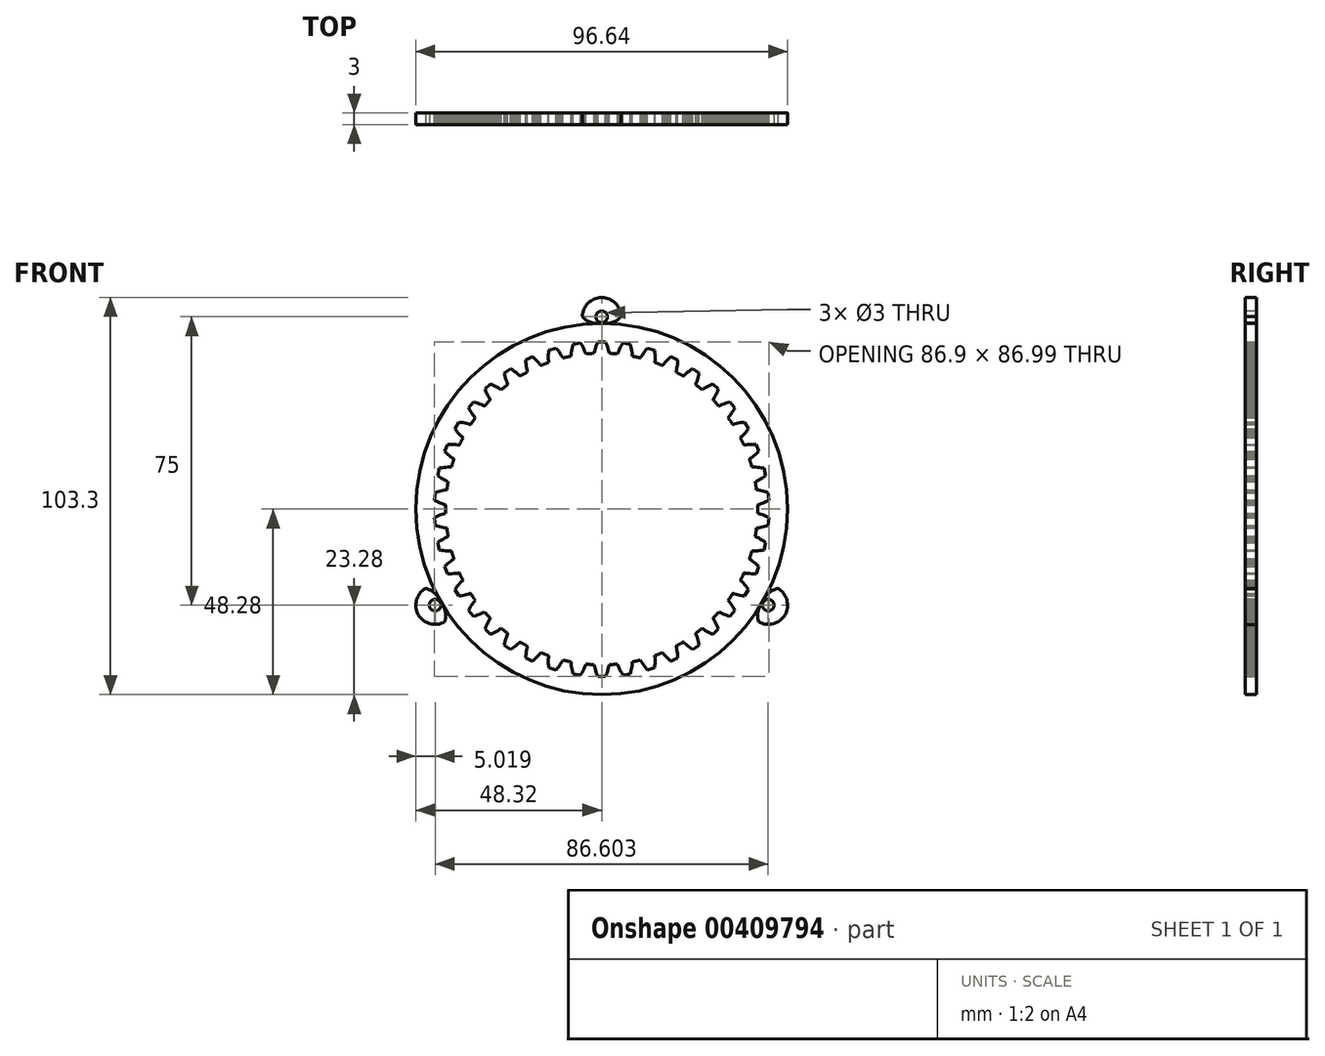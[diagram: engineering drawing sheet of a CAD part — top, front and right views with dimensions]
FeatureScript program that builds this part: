
annotation { "Feature Type Name" : "Feature", "Feature Type Description" : "" }
export const myFeature = defineFeature(function(context is Context, id is Id, definition is map)
    precondition{}
    {
        {
            var Q0;
            Q0=qCreatedBy(makeId("Front.planeOp"),FACE);
            var sketch = newSketch(context, id + "F0", { "sketchPlane" : qUnion([Q0])});
            skLineSegment(sketch, "E0", {"start": v(-40.42, 1.05) * mm, "end": v(-40.54, 1.09) * mm});
            skLineSegment(sketch, "E1", {"start": v(-40.54, 1.09) * mm, "end": v(-40.67, 1.12) * mm});
            skLineSegment(sketch, "E2", {"start": v(-40.67, 1.12) * mm, "end": v(-40.92, 1.2) * mm});
            skLineSegment(sketch, "E3", {"start": v(-40.92, 1.2) * mm, "end": v(-41.43, 1.36) * mm});
            skLineSegment(sketch, "E4", {"start": v(-41.43, 1.36) * mm, "end": v(-41.94, 1.56) * mm});
            skLineSegment(sketch, "E5", {"start": v(-41.94, 1.56) * mm, "end": v(-42.44, 1.77) * mm});
            skLineSegment(sketch, "E6", {"start": v(-42.44, 1.77) * mm, "end": v(-42.95, 2) * mm});
            skLineSegment(sketch, "E7", {"start": v(-42.95, 2) * mm, "end": v(-43.45, 2.26) * mm});
            skLineSegment(sketch, "E8", {"start": v(-43.45, 2.26) * mm, "end": v(-43.3, 4.24) * mm});
            skLineSegment(sketch, "E9", {"start": v(-43.3, 4.24) * mm, "end": v(-42.77, 4.42) * mm});
            skLineSegment(sketch, "E10", {"start": v(-42.77, 4.42) * mm, "end": v(-42.23, 4.57) * mm});
            skLineSegment(sketch, "E11", {"start": v(-42.23, 4.57) * mm, "end": v(-41.7, 4.71) * mm});
            skLineSegment(sketch, "E12", {"start": v(-41.7, 4.71) * mm, "end": v(-41.17, 4.83) * mm});
            skLineSegment(sketch, "E13", {"start": v(-41.17, 4.83) * mm, "end": v(-40.65, 4.92) * mm});
            skLineSegment(sketch, "E14", {"start": v(-40.65, 4.92) * mm, "end": v(-40.38, 4.95) * mm});
            skLineSegment(sketch, "E15", {"start": v(-40.38, 4.95) * mm, "end": v(-40.25, 4.97) * mm});
            skLineSegment(sketch, "E16", {"start": v(-40.25, 4.97) * mm, "end": v(-40.12, 4.98) * mm});
            skLineSegment(sketch, "E17", {"start": v(-40.12, 4.98) * mm, "end": v(-39.8, 7.06) * mm});
            skLineSegment(sketch, "E18", {"start": v(-39.8, 7.06) * mm, "end": v(-39.93, 7.12) * mm});
            skLineSegment(sketch, "E19", {"start": v(-39.93, 7.12) * mm, "end": v(-40.05, 7.17) * mm});
            skLineSegment(sketch, "E20", {"start": v(-40.05, 7.17) * mm, "end": v(-40.29, 7.28) * mm});
            skLineSegment(sketch, "E21", {"start": v(-40.29, 7.28) * mm, "end": v(-40.77, 7.52) * mm});
            skLineSegment(sketch, "E22", {"start": v(-40.77, 7.52) * mm, "end": v(-41.24, 7.8) * mm});
            skLineSegment(sketch, "E23", {"start": v(-41.24, 7.8) * mm, "end": v(-41.7, 8.08) * mm});
            skLineSegment(sketch, "E24", {"start": v(-41.7, 8.08) * mm, "end": v(-42.17, 8.39) * mm});
            skLineSegment(sketch, "E25", {"start": v(-42.17, 8.39) * mm, "end": v(-42.63, 8.71) * mm});
            skLineSegment(sketch, "E26", {"start": v(-42.63, 8.71) * mm, "end": v(-42.19, 10.64) * mm});
            skLineSegment(sketch, "E27", {"start": v(-42.19, 10.64) * mm, "end": v(-41.63, 10.74) * mm});
            skLineSegment(sketch, "E28", {"start": v(-41.63, 10.74) * mm, "end": v(-41.08, 10.82) * mm});
            skLineSegment(sketch, "E29", {"start": v(-41.08, 10.82) * mm, "end": v(-40.54, 10.87) * mm});
            skLineSegment(sketch, "E30", {"start": v(-40.54, 10.87) * mm, "end": v(-40, 10.9) * mm});
            skLineSegment(sketch, "E31", {"start": v(-40, 10.9) * mm, "end": v(-39.46, 10.92) * mm});
            skLineSegment(sketch, "E32", {"start": v(-39.46, 10.92) * mm, "end": v(-39.2, 10.92) * mm});
            skLineSegment(sketch, "E33", {"start": v(-39.2, 10.92) * mm, "end": v(-39.06, 10.91) * mm});
            skLineSegment(sketch, "E34", {"start": v(-39.06, 10.91) * mm, "end": v(-38.93, 10.9) * mm});
            skLineSegment(sketch, "E35", {"start": v(-38.93, 10.9) * mm, "end": v(-38.3, 12.92) * mm});
            skLineSegment(sketch, "E36", {"start": v(-38.3, 12.92) * mm, "end": v(-38.42, 12.99) * mm});
            skLineSegment(sketch, "E37", {"start": v(-38.42, 12.99) * mm, "end": v(-38.53, 13.06) * mm});
            skLineSegment(sketch, "E38", {"start": v(-38.53, 13.06) * mm, "end": v(-38.75, 13.2) * mm});
            skLineSegment(sketch, "E39", {"start": v(-38.75, 13.2) * mm, "end": v(-39.19, 13.52) * mm});
            skLineSegment(sketch, "E40", {"start": v(-39.19, 13.52) * mm, "end": v(-39.62, 13.85) * mm});
            skLineSegment(sketch, "E41", {"start": v(-39.62, 13.85) * mm, "end": v(-40.04, 14.2) * mm});
            skLineSegment(sketch, "E42", {"start": v(-40.04, 14.2) * mm, "end": v(-40.45, 14.58) * mm});
            skLineSegment(sketch, "E43", {"start": v(-40.45, 14.58) * mm, "end": v(-40.85, 14.97) * mm});
            skLineSegment(sketch, "E44", {"start": v(-40.85, 14.97) * mm, "end": v(-40.13, 16.81) * mm});
            skLineSegment(sketch, "E45", {"start": v(-40.13, 16.81) * mm, "end": v(-39.57, 16.82) * mm});
            skLineSegment(sketch, "E46", {"start": v(-39.57, 16.82) * mm, "end": v(-39.01, 16.82) * mm});
            skLineSegment(sketch, "E47", {"start": v(-39.01, 16.82) * mm, "end": v(-38.46, 16.8) * mm});
            skLineSegment(sketch, "E48", {"start": v(-38.46, 16.8) * mm, "end": v(-37.92, 16.75) * mm});
            skLineSegment(sketch, "E49", {"start": v(-37.92, 16.75) * mm, "end": v(-37.4, 16.68) * mm});
            skLineSegment(sketch, "E50", {"start": v(-37.4, 16.68) * mm, "end": v(-37.13, 16.64) * mm});
            skLineSegment(sketch, "E51", {"start": v(-37.13, 16.64) * mm, "end": v(-37, 16.61) * mm});
            skLineSegment(sketch, "E52", {"start": v(-37, 16.61) * mm, "end": v(-36.87, 16.59) * mm});
            skLineSegment(sketch, "E53", {"start": v(-36.87, 16.59) * mm, "end": v(-35.96, 18.48) * mm});
            skLineSegment(sketch, "E54", {"start": v(-35.96, 18.48) * mm, "end": v(-36.06, 18.57) * mm});
            skLineSegment(sketch, "E55", {"start": v(-36.06, 18.57) * mm, "end": v(-36.16, 18.66) * mm});
            skLineSegment(sketch, "E56", {"start": v(-36.16, 18.66) * mm, "end": v(-36.35, 18.83) * mm});
            skLineSegment(sketch, "E57", {"start": v(-36.35, 18.83) * mm, "end": v(-36.74, 19.2) * mm});
            skLineSegment(sketch, "E58", {"start": v(-36.74, 19.2) * mm, "end": v(-37.11, 19.6) * mm});
            skLineSegment(sketch, "E59", {"start": v(-37.11, 19.6) * mm, "end": v(-37.47, 20.01) * mm});
            skLineSegment(sketch, "E60", {"start": v(-37.47, 20.01) * mm, "end": v(-37.82, 20.44) * mm});
            skLineSegment(sketch, "E61", {"start": v(-37.82, 20.44) * mm, "end": v(-38.16, 20.9) * mm});
            skLineSegment(sketch, "E62", {"start": v(-38.16, 20.9) * mm, "end": v(-37.17, 22.6) * mm});
            skLineSegment(sketch, "E63", {"start": v(-37.17, 22.6) * mm, "end": v(-36.62, 22.53) * mm});
            skLineSegment(sketch, "E64", {"start": v(-36.62, 22.53) * mm, "end": v(-36.07, 22.44) * mm});
            skLineSegment(sketch, "E65", {"start": v(-36.07, 22.44) * mm, "end": v(-35.53, 22.34) * mm});
            skLineSegment(sketch, "E66", {"start": v(-35.53, 22.34) * mm, "end": v(-35, 22.21) * mm});
            skLineSegment(sketch, "E67", {"start": v(-35, 22.21) * mm, "end": v(-34.49, 22.07) * mm});
            skLineSegment(sketch, "E68", {"start": v(-34.49, 22.07) * mm, "end": v(-34.23, 21.98) * mm});
            skLineSegment(sketch, "E69", {"start": v(-34.23, 21.98) * mm, "end": v(-34.1, 21.94) * mm});
            skLineSegment(sketch, "E70", {"start": v(-34.1, 21.94) * mm, "end": v(-33.99, 21.9) * mm});
            skLineSegment(sketch, "E71", {"start": v(-33.99, 21.9) * mm, "end": v(-32.8, 23.64) * mm});
            skLineSegment(sketch, "E72", {"start": v(-32.8, 23.64) * mm, "end": v(-32.89, 23.74) * mm});
            skLineSegment(sketch, "E73", {"start": v(-32.89, 23.74) * mm, "end": v(-32.97, 23.84) * mm});
            skLineSegment(sketch, "E74", {"start": v(-32.97, 23.84) * mm, "end": v(-33.14, 24.04) * mm});
            skLineSegment(sketch, "E75", {"start": v(-33.14, 24.04) * mm, "end": v(-33.46, 24.47) * mm});
            skLineSegment(sketch, "E76", {"start": v(-33.46, 24.47) * mm, "end": v(-33.77, 24.91) * mm});
            skLineSegment(sketch, "E77", {"start": v(-33.77, 24.91) * mm, "end": v(-34.07, 25.37) * mm});
            skLineSegment(sketch, "E78", {"start": v(-34.07, 25.37) * mm, "end": v(-34.35, 25.85) * mm});
            skLineSegment(sketch, "E79", {"start": v(-34.35, 25.85) * mm, "end": v(-34.62, 26.35) * mm});
            skLineSegment(sketch, "E80", {"start": v(-34.62, 26.35) * mm, "end": v(-33.39, 27.9) * mm});
            skLineSegment(sketch, "E81", {"start": v(-33.39, 27.9) * mm, "end": v(-32.85, 27.74) * mm});
            skLineSegment(sketch, "E82", {"start": v(-32.85, 27.74) * mm, "end": v(-32.32, 27.57) * mm});
            skLineSegment(sketch, "E83", {"start": v(-32.32, 27.57) * mm, "end": v(-31.8, 27.38) * mm});
            skLineSegment(sketch, "E84", {"start": v(-31.8, 27.38) * mm, "end": v(-31.3, 27.18) * mm});
            skLineSegment(sketch, "E85", {"start": v(-31.3, 27.18) * mm, "end": v(-30.81, 26.96) * mm});
            skLineSegment(sketch, "E86", {"start": v(-30.81, 26.96) * mm, "end": v(-30.58, 26.84) * mm});
            skLineSegment(sketch, "E87", {"start": v(-30.58, 26.84) * mm, "end": v(-30.46, 26.78) * mm});
            skLineSegment(sketch, "E88", {"start": v(-30.46, 26.78) * mm, "end": v(-30.34, 26.72) * mm});
            skLineSegment(sketch, "E89", {"start": v(-30.34, 26.72) * mm, "end": v(-28.91, 28.26) * mm});
            skLineSegment(sketch, "E90", {"start": v(-28.91, 28.26) * mm, "end": v(-28.98, 28.37) * mm});
            skLineSegment(sketch, "E91", {"start": v(-28.98, 28.37) * mm, "end": v(-29.05, 28.48) * mm});
            skLineSegment(sketch, "E92", {"start": v(-29.05, 28.48) * mm, "end": v(-29.19, 28.71) * mm});
            skLineSegment(sketch, "E93", {"start": v(-29.19, 28.71) * mm, "end": v(-29.44, 29.18) * mm});
            skLineSegment(sketch, "E94", {"start": v(-29.44, 29.18) * mm, "end": v(-29.68, 29.67) * mm});
            skLineSegment(sketch, "E95", {"start": v(-29.68, 29.67) * mm, "end": v(-29.9, 30.17) * mm});
            skLineSegment(sketch, "E96", {"start": v(-29.9, 30.17) * mm, "end": v(-30.12, 30.68) * mm});
            skLineSegment(sketch, "E97", {"start": v(-30.12, 30.68) * mm, "end": v(-30.31, 31.21) * mm});
            skLineSegment(sketch, "E98", {"start": v(-30.31, 31.21) * mm, "end": v(-28.86, 32.56) * mm});
            skLineSegment(sketch, "E99", {"start": v(-28.86, 32.56) * mm, "end": v(-28.35, 32.33) * mm});
            skLineSegment(sketch, "E100", {"start": v(-28.35, 32.33) * mm, "end": v(-27.85, 32.08) * mm});
            skLineSegment(sketch, "E101", {"start": v(-27.85, 32.08) * mm, "end": v(-27.37, 31.82) * mm});
            skLineSegment(sketch, "E102", {"start": v(-27.37, 31.82) * mm, "end": v(-26.9, 31.54) * mm});
            skLineSegment(sketch, "E103", {"start": v(-26.9, 31.54) * mm, "end": v(-26.45, 31.25) * mm});
            skLineSegment(sketch, "E104", {"start": v(-26.45, 31.25) * mm, "end": v(-26.23, 31.1) * mm});
            skLineSegment(sketch, "E105", {"start": v(-26.23, 31.1) * mm, "end": v(-26.13, 31.02) * mm});
            skLineSegment(sketch, "E106", {"start": v(-26.13, 31.02) * mm, "end": v(-26.02, 30.94) * mm});
            skLineSegment(sketch, "E107", {"start": v(-26.02, 30.94) * mm, "end": v(-24.38, 32.25) * mm});
            skLineSegment(sketch, "E108", {"start": v(-24.38, 32.25) * mm, "end": v(-24.43, 32.37) * mm});
            skLineSegment(sketch, "E109", {"start": v(-24.43, 32.37) * mm, "end": v(-24.48, 32.5) * mm});
            skLineSegment(sketch, "E110", {"start": v(-24.48, 32.5) * mm, "end": v(-24.58, 32.74) * mm});
            skLineSegment(sketch, "E111", {"start": v(-24.58, 32.74) * mm, "end": v(-24.77, 33.24) * mm});
            skLineSegment(sketch, "E112", {"start": v(-24.77, 33.24) * mm, "end": v(-24.93, 33.76) * mm});
            skLineSegment(sketch, "E113", {"start": v(-24.93, 33.76) * mm, "end": v(-25.08, 34.29) * mm});
            skLineSegment(sketch, "E114", {"start": v(-25.08, 34.29) * mm, "end": v(-25.2, 34.83) * mm});
            skLineSegment(sketch, "E115", {"start": v(-25.2, 34.83) * mm, "end": v(-25.32, 35.38) * mm});
            skLineSegment(sketch, "E116", {"start": v(-25.32, 35.38) * mm, "end": v(-23.68, 36.5) * mm});
            skLineSegment(sketch, "E117", {"start": v(-23.68, 36.5) * mm, "end": v(-23.21, 36.19) * mm});
            skLineSegment(sketch, "E118", {"start": v(-23.21, 36.19) * mm, "end": v(-22.76, 35.87) * mm});
            skLineSegment(sketch, "E119", {"start": v(-22.76, 35.87) * mm, "end": v(-22.32, 35.54) * mm});
            skLineSegment(sketch, "E120", {"start": v(-22.32, 35.54) * mm, "end": v(-21.9, 35.2) * mm});
            skLineSegment(sketch, "E121", {"start": v(-21.9, 35.2) * mm, "end": v(-21.5, 34.84) * mm});
            skLineSegment(sketch, "E122", {"start": v(-21.5, 34.84) * mm, "end": v(-21.3, 34.66) * mm});
            skLineSegment(sketch, "E123", {"start": v(-21.3, 34.66) * mm, "end": v(-21.21, 34.57) * mm});
            skLineSegment(sketch, "E124", {"start": v(-21.21, 34.57) * mm, "end": v(-21.12, 34.47) * mm});
            skLineSegment(sketch, "E125", {"start": v(-21.12, 34.47) * mm, "end": v(-19.3, 35.53) * mm});
            skLineSegment(sketch, "E126", {"start": v(-19.3, 35.53) * mm, "end": v(-19.33, 35.65) * mm});
            skLineSegment(sketch, "E127", {"start": v(-19.33, 35.65) * mm, "end": v(-19.36, 35.78) * mm});
            skLineSegment(sketch, "E128", {"start": v(-19.36, 35.78) * mm, "end": v(-19.43, 36.04) * mm});
            skLineSegment(sketch, "E129", {"start": v(-19.43, 36.04) * mm, "end": v(-19.53, 36.56) * mm});
            skLineSegment(sketch, "E130", {"start": v(-19.53, 36.56) * mm, "end": v(-19.62, 37.1) * mm});
            skLineSegment(sketch, "E131", {"start": v(-19.62, 37.1) * mm, "end": v(-19.69, 37.64) * mm});
            skLineSegment(sketch, "E132", {"start": v(-19.69, 37.64) * mm, "end": v(-19.73, 38.2) * mm});
            skLineSegment(sketch, "E133", {"start": v(-19.73, 38.2) * mm, "end": v(-19.76, 38.76) * mm});
            skLineSegment(sketch, "E134", {"start": v(-19.76, 38.76) * mm, "end": v(-17.98, 39.62) * mm});
            skLineSegment(sketch, "E135", {"start": v(-17.98, 39.62) * mm, "end": v(-17.56, 39.24) * mm});
            skLineSegment(sketch, "E136", {"start": v(-17.56, 39.24) * mm, "end": v(-17.16, 38.86) * mm});
            skLineSegment(sketch, "E137", {"start": v(-17.16, 38.86) * mm, "end": v(-16.77, 38.47) * mm});
            skLineSegment(sketch, "E138", {"start": v(-16.77, 38.47) * mm, "end": v(-16.4, 38.07) * mm});
            skLineSegment(sketch, "E139", {"start": v(-16.4, 38.07) * mm, "end": v(-16.06, 37.66) * mm});
            skLineSegment(sketch, "E140", {"start": v(-16.06, 37.66) * mm, "end": v(-15.9, 37.45) * mm});
            skLineSegment(sketch, "E141", {"start": v(-15.9, 37.45) * mm, "end": v(-15.82, 37.34) * mm});
            skLineSegment(sketch, "E142", {"start": v(-15.82, 37.34) * mm, "end": v(-15.75, 37.24) * mm});
            skLineSegment(sketch, "E143", {"start": v(-15.75, 37.24) * mm, "end": v(-13.79, 38) * mm});
            skLineSegment(sketch, "E144", {"start": v(-13.79, 38) * mm, "end": v(-13.8, 38.14) * mm});
            skLineSegment(sketch, "E145", {"start": v(-13.8, 38.14) * mm, "end": v(-13.82, 38.27) * mm});
            skLineSegment(sketch, "E146", {"start": v(-13.82, 38.27) * mm, "end": v(-13.84, 38.53) * mm});
            skLineSegment(sketch, "E147", {"start": v(-13.84, 38.53) * mm, "end": v(-13.87, 39.07) * mm});
            skLineSegment(sketch, "E148", {"start": v(-13.87, 39.07) * mm, "end": v(-13.87, 39.6) * mm});
            skLineSegment(sketch, "E149", {"start": v(-13.87, 39.6) * mm, "end": v(-13.86, 40.16) * mm});
            skLineSegment(sketch, "E150", {"start": v(-13.86, 40.16) * mm, "end": v(-13.82, 40.71) * mm});
            skLineSegment(sketch, "E151", {"start": v(-13.82, 40.71) * mm, "end": v(-13.77, 41.27) * mm});
            skLineSegment(sketch, "E152", {"start": v(-13.77, 41.27) * mm, "end": v(-11.87, 41.86) * mm});
            skLineSegment(sketch, "E153", {"start": v(-11.87, 41.86) * mm, "end": v(-11.51, 41.42) * mm});
            skLineSegment(sketch, "E154", {"start": v(-11.51, 41.42) * mm, "end": v(-11.17, 40.99) * mm});
            skLineSegment(sketch, "E155", {"start": v(-11.17, 40.99) * mm, "end": v(-10.85, 40.54) * mm});
            skLineSegment(sketch, "E156", {"start": v(-10.85, 40.54) * mm, "end": v(-10.55, 40.1) * mm});
            skLineSegment(sketch, "E157", {"start": v(-10.55, 40.1) * mm, "end": v(-10.27, 39.63) * mm});
            skLineSegment(sketch, "E158", {"start": v(-10.27, 39.63) * mm, "end": v(-10.14, 39.4) * mm});
            skLineSegment(sketch, "E159", {"start": v(-10.14, 39.4) * mm, "end": v(-10.08, 39.28) * mm});
            skLineSegment(sketch, "E160", {"start": v(-10.08, 39.28) * mm, "end": v(-10.02, 39.17) * mm});
            skLineSegment(sketch, "E161", {"start": v(-10.02, 39.17) * mm, "end": v(-7.97, 39.64) * mm});
            skLineSegment(sketch, "E162", {"start": v(-7.97, 39.64) * mm, "end": v(-7.96, 39.77) * mm});
            skLineSegment(sketch, "E163", {"start": v(-7.96, 39.77) * mm, "end": v(-7.96, 39.9) * mm});
            skLineSegment(sketch, "E164", {"start": v(-7.96, 39.9) * mm, "end": v(-7.94, 40.16) * mm});
            skLineSegment(sketch, "E165", {"start": v(-7.94, 40.16) * mm, "end": v(-7.89, 40.7) * mm});
            skLineSegment(sketch, "E166", {"start": v(-7.89, 40.7) * mm, "end": v(-7.81, 41.23) * mm});
            skLineSegment(sketch, "E167", {"start": v(-7.81, 41.23) * mm, "end": v(-7.72, 41.77) * mm});
            skLineSegment(sketch, "E168", {"start": v(-7.72, 41.77) * mm, "end": v(-7.6, 42.32) * mm});
            skLineSegment(sketch, "E169", {"start": v(-7.6, 42.32) * mm, "end": v(-7.46, 42.86) * mm});
            skLineSegment(sketch, "E170", {"start": v(-7.46, 42.86) * mm, "end": v(-5.5, 43.16) * mm});
            skLineSegment(sketch, "E171", {"start": v(-5.5, 43.16) * mm, "end": v(-5.21, 42.68) * mm});
            skLineSegment(sketch, "E172", {"start": v(-5.21, 42.68) * mm, "end": v(-4.94, 42.2) * mm});
            skLineSegment(sketch, "E173", {"start": v(-4.94, 42.2) * mm, "end": v(-4.69, 41.7) * mm});
            skLineSegment(sketch, "E174", {"start": v(-4.69, 41.7) * mm, "end": v(-4.46, 41.21) * mm});
            skLineSegment(sketch, "E175", {"start": v(-4.46, 41.21) * mm, "end": v(-4.25, 40.72) * mm});
            skLineSegment(sketch, "E176", {"start": v(-4.25, 40.72) * mm, "end": v(-4.16, 40.47) * mm});
            skLineSegment(sketch, "E177", {"start": v(-4.16, 40.47) * mm, "end": v(-4.11, 40.35) * mm});
            skLineSegment(sketch, "E178", {"start": v(-4.11, 40.35) * mm, "end": v(-4.07, 40.22) * mm});
            skLineSegment(sketch, "E179", {"start": v(-4.07, 40.22) * mm, "end": v(-1.97, 40.38) * mm});
            skLineSegment(sketch, "E180", {"start": v(-1.97, 40.38) * mm, "end": v(-1.95, 40.51) * mm});
            skLineSegment(sketch, "E181", {"start": v(-1.95, 40.51) * mm, "end": v(-1.92, 40.64) * mm});
            skLineSegment(sketch, "E182", {"start": v(-1.92, 40.64) * mm, "end": v(-1.87, 40.9) * mm});
            skLineSegment(sketch, "E183", {"start": v(-1.87, 40.9) * mm, "end": v(-1.74, 41.42) * mm});
            skLineSegment(sketch, "E184", {"start": v(-1.74, 41.42) * mm, "end": v(-1.58, 41.94) * mm});
            skLineSegment(sketch, "E185", {"start": v(-1.58, 41.94) * mm, "end": v(-1.4, 42.46) * mm});
            skLineSegment(sketch, "E186", {"start": v(-1.4, 42.46) * mm, "end": v(-1.2, 42.98) * mm});
            skLineSegment(sketch, "E187", {"start": v(-1.2, 42.98) * mm, "end": v(-0.99, 43.5) * mm});
            skLineSegment(sketch, "E188", {"start": v(-0.99, 43.5) * mm, "end": v(0.99, 43.5) * mm});
            skLineSegment(sketch, "E189", {"start": v(0.99, 43.5) * mm, "end": v(1.2, 42.98) * mm});
            skLineSegment(sketch, "E190", {"start": v(1.2, 42.98) * mm, "end": v(1.4, 42.46) * mm});
            skLineSegment(sketch, "E191", {"start": v(1.4, 42.46) * mm, "end": v(1.58, 41.94) * mm});
            skLineSegment(sketch, "E192", {"start": v(1.58, 41.94) * mm, "end": v(1.74, 41.42) * mm});
            skLineSegment(sketch, "E193", {"start": v(1.74, 41.42) * mm, "end": v(1.87, 40.9) * mm});
            skLineSegment(sketch, "E194", {"start": v(1.87, 40.9) * mm, "end": v(1.92, 40.64) * mm});
            skLineSegment(sketch, "E195", {"start": v(1.92, 40.64) * mm, "end": v(1.95, 40.51) * mm});
            skLineSegment(sketch, "E196", {"start": v(1.95, 40.51) * mm, "end": v(1.97, 40.38) * mm});
            skLineSegment(sketch, "E197", {"start": v(1.97, 40.38) * mm, "end": v(4.07, 40.22) * mm});
            skLineSegment(sketch, "E198", {"start": v(4.07, 40.22) * mm, "end": v(4.11, 40.35) * mm});
            skLineSegment(sketch, "E199", {"start": v(4.11, 40.35) * mm, "end": v(4.16, 40.47) * mm});
            skLineSegment(sketch, "E200", {"start": v(4.16, 40.47) * mm, "end": v(4.25, 40.72) * mm});
            skLineSegment(sketch, "E201", {"start": v(4.25, 40.72) * mm, "end": v(4.46, 41.21) * mm});
            skLineSegment(sketch, "E202", {"start": v(4.46, 41.21) * mm, "end": v(4.69, 41.7) * mm});
            skLineSegment(sketch, "E203", {"start": v(4.69, 41.7) * mm, "end": v(4.94, 42.2) * mm});
            skLineSegment(sketch, "E204", {"start": v(4.94, 42.2) * mm, "end": v(5.21, 42.68) * mm});
            skLineSegment(sketch, "E205", {"start": v(5.21, 42.68) * mm, "end": v(5.5, 43.16) * mm});
            skLineSegment(sketch, "E206", {"start": v(5.5, 43.16) * mm, "end": v(7.46, 42.86) * mm});
            skLineSegment(sketch, "E207", {"start": v(7.46, 42.86) * mm, "end": v(7.6, 42.32) * mm});
            skLineSegment(sketch, "E208", {"start": v(7.6, 42.32) * mm, "end": v(7.72, 41.77) * mm});
            skLineSegment(sketch, "E209", {"start": v(7.72, 41.77) * mm, "end": v(7.81, 41.23) * mm});
            skLineSegment(sketch, "E210", {"start": v(7.81, 41.23) * mm, "end": v(7.89, 40.7) * mm});
            skLineSegment(sketch, "E211", {"start": v(7.89, 40.7) * mm, "end": v(7.94, 40.16) * mm});
            skLineSegment(sketch, "E212", {"start": v(7.94, 40.16) * mm, "end": v(7.96, 39.9) * mm});
            skLineSegment(sketch, "E213", {"start": v(7.96, 39.9) * mm, "end": v(7.96, 39.77) * mm});
            skLineSegment(sketch, "E214", {"start": v(7.96, 39.77) * mm, "end": v(7.97, 39.64) * mm});
            skLineSegment(sketch, "E215", {"start": v(7.97, 39.64) * mm, "end": v(10.02, 39.17) * mm});
            skLineSegment(sketch, "E216", {"start": v(10.02, 39.17) * mm, "end": v(10.08, 39.28) * mm});
            skLineSegment(sketch, "E217", {"start": v(10.08, 39.28) * mm, "end": v(10.14, 39.4) * mm});
            skLineSegment(sketch, "E218", {"start": v(10.14, 39.4) * mm, "end": v(10.27, 39.63) * mm});
            skLineSegment(sketch, "E219", {"start": v(10.27, 39.63) * mm, "end": v(10.55, 40.1) * mm});
            skLineSegment(sketch, "E220", {"start": v(10.55, 40.1) * mm, "end": v(10.85, 40.54) * mm});
            skLineSegment(sketch, "E221", {"start": v(10.85, 40.54) * mm, "end": v(11.17, 40.99) * mm});
            skLineSegment(sketch, "E222", {"start": v(11.17, 40.99) * mm, "end": v(11.51, 41.42) * mm});
            skLineSegment(sketch, "E223", {"start": v(11.51, 41.42) * mm, "end": v(11.87, 41.86) * mm});
            skLineSegment(sketch, "E224", {"start": v(11.87, 41.86) * mm, "end": v(13.77, 41.27) * mm});
            skLineSegment(sketch, "E225", {"start": v(13.77, 41.27) * mm, "end": v(13.82, 40.71) * mm});
            skLineSegment(sketch, "E226", {"start": v(13.82, 40.71) * mm, "end": v(13.86, 40.16) * mm});
            skLineSegment(sketch, "E227", {"start": v(13.86, 40.16) * mm, "end": v(13.87, 39.6) * mm});
            skLineSegment(sketch, "E228", {"start": v(13.87, 39.6) * mm, "end": v(13.87, 39.07) * mm});
            skLineSegment(sketch, "E229", {"start": v(13.87, 39.07) * mm, "end": v(13.84, 38.53) * mm});
            skLineSegment(sketch, "E230", {"start": v(13.84, 38.53) * mm, "end": v(13.82, 38.27) * mm});
            skLineSegment(sketch, "E231", {"start": v(13.82, 38.27) * mm, "end": v(13.8, 38.14) * mm});
            skLineSegment(sketch, "E232", {"start": v(13.8, 38.14) * mm, "end": v(13.79, 38) * mm});
            skLineSegment(sketch, "E233", {"start": v(13.79, 38) * mm, "end": v(15.75, 37.24) * mm});
            skLineSegment(sketch, "E234", {"start": v(15.75, 37.24) * mm, "end": v(15.82, 37.34) * mm});
            skLineSegment(sketch, "E235", {"start": v(15.82, 37.34) * mm, "end": v(15.9, 37.45) * mm});
            skLineSegment(sketch, "E236", {"start": v(15.9, 37.45) * mm, "end": v(16.06, 37.66) * mm});
            skLineSegment(sketch, "E237", {"start": v(16.06, 37.66) * mm, "end": v(16.4, 38.07) * mm});
            skLineSegment(sketch, "E238", {"start": v(16.4, 38.07) * mm, "end": v(16.77, 38.47) * mm});
            skLineSegment(sketch, "E239", {"start": v(16.77, 38.47) * mm, "end": v(17.16, 38.86) * mm});
            skLineSegment(sketch, "E240", {"start": v(17.16, 38.86) * mm, "end": v(17.56, 39.24) * mm});
            skLineSegment(sketch, "E241", {"start": v(17.56, 39.24) * mm, "end": v(17.98, 39.62) * mm});
            skLineSegment(sketch, "E242", {"start": v(17.98, 39.62) * mm, "end": v(19.76, 38.76) * mm});
            skLineSegment(sketch, "E243", {"start": v(19.76, 38.76) * mm, "end": v(19.73, 38.2) * mm});
            skLineSegment(sketch, "E244", {"start": v(19.73, 38.2) * mm, "end": v(19.69, 37.64) * mm});
            skLineSegment(sketch, "E245", {"start": v(19.69, 37.64) * mm, "end": v(19.62, 37.1) * mm});
            skLineSegment(sketch, "E246", {"start": v(19.62, 37.1) * mm, "end": v(19.53, 36.56) * mm});
            skLineSegment(sketch, "E247", {"start": v(19.53, 36.56) * mm, "end": v(19.43, 36.04) * mm});
            skLineSegment(sketch, "E248", {"start": v(19.43, 36.04) * mm, "end": v(19.36, 35.78) * mm});
            skLineSegment(sketch, "E249", {"start": v(19.36, 35.78) * mm, "end": v(19.33, 35.65) * mm});
            skLineSegment(sketch, "E250", {"start": v(19.33, 35.65) * mm, "end": v(19.3, 35.53) * mm});
            skLineSegment(sketch, "E251", {"start": v(19.3, 35.53) * mm, "end": v(21.12, 34.47) * mm});
            skLineSegment(sketch, "E252", {"start": v(21.12, 34.47) * mm, "end": v(21.21, 34.57) * mm});
            skLineSegment(sketch, "E253", {"start": v(21.21, 34.57) * mm, "end": v(21.3, 34.66) * mm});
            skLineSegment(sketch, "E254", {"start": v(21.3, 34.66) * mm, "end": v(21.5, 34.84) * mm});
            skLineSegment(sketch, "E255", {"start": v(21.5, 34.84) * mm, "end": v(21.9, 35.2) * mm});
            skLineSegment(sketch, "E256", {"start": v(21.9, 35.2) * mm, "end": v(22.32, 35.54) * mm});
            skLineSegment(sketch, "E257", {"start": v(22.32, 35.54) * mm, "end": v(22.76, 35.87) * mm});
            skLineSegment(sketch, "E258", {"start": v(22.76, 35.87) * mm, "end": v(23.21, 36.19) * mm});
            skLineSegment(sketch, "E259", {"start": v(23.21, 36.19) * mm, "end": v(23.68, 36.5) * mm});
            skLineSegment(sketch, "E260", {"start": v(23.68, 36.5) * mm, "end": v(25.32, 35.38) * mm});
            skLineSegment(sketch, "E261", {"start": v(25.32, 35.38) * mm, "end": v(25.2, 34.83) * mm});
            skLineSegment(sketch, "E262", {"start": v(25.2, 34.83) * mm, "end": v(25.08, 34.29) * mm});
            skLineSegment(sketch, "E263", {"start": v(25.08, 34.29) * mm, "end": v(24.93, 33.76) * mm});
            skLineSegment(sketch, "E264", {"start": v(24.93, 33.76) * mm, "end": v(24.77, 33.24) * mm});
            skLineSegment(sketch, "E265", {"start": v(24.77, 33.24) * mm, "end": v(24.58, 32.74) * mm});
            skLineSegment(sketch, "E266", {"start": v(24.58, 32.74) * mm, "end": v(24.48, 32.5) * mm});
            skLineSegment(sketch, "E267", {"start": v(24.48, 32.5) * mm, "end": v(24.43, 32.37) * mm});
            skLineSegment(sketch, "E268", {"start": v(24.43, 32.37) * mm, "end": v(24.38, 32.25) * mm});
            skLineSegment(sketch, "E269", {"start": v(24.38, 32.25) * mm, "end": v(26.02, 30.94) * mm});
            skLineSegment(sketch, "E270", {"start": v(26.02, 30.94) * mm, "end": v(26.13, 31.02) * mm});
            skLineSegment(sketch, "E271", {"start": v(26.13, 31.02) * mm, "end": v(26.23, 31.1) * mm});
            skLineSegment(sketch, "E272", {"start": v(26.23, 31.1) * mm, "end": v(26.45, 31.25) * mm});
            skLineSegment(sketch, "E273", {"start": v(26.45, 31.25) * mm, "end": v(26.9, 31.54) * mm});
            skLineSegment(sketch, "E274", {"start": v(26.9, 31.54) * mm, "end": v(27.37, 31.82) * mm});
            skLineSegment(sketch, "E275", {"start": v(27.37, 31.82) * mm, "end": v(27.85, 32.08) * mm});
            skLineSegment(sketch, "E276", {"start": v(27.85, 32.08) * mm, "end": v(28.35, 32.33) * mm});
            skLineSegment(sketch, "E277", {"start": v(28.35, 32.33) * mm, "end": v(28.86, 32.56) * mm});
            skLineSegment(sketch, "E278", {"start": v(28.86, 32.56) * mm, "end": v(30.31, 31.21) * mm});
            skLineSegment(sketch, "E279", {"start": v(30.31, 31.21) * mm, "end": v(30.12, 30.68) * mm});
            skLineSegment(sketch, "E280", {"start": v(30.12, 30.68) * mm, "end": v(29.9, 30.17) * mm});
            skLineSegment(sketch, "E281", {"start": v(29.9, 30.17) * mm, "end": v(29.68, 29.67) * mm});
            skLineSegment(sketch, "E282", {"start": v(29.68, 29.67) * mm, "end": v(29.44, 29.18) * mm});
            skLineSegment(sketch, "E283", {"start": v(29.44, 29.18) * mm, "end": v(29.19, 28.71) * mm});
            skLineSegment(sketch, "E284", {"start": v(29.19, 28.71) * mm, "end": v(29.05, 28.48) * mm});
            skLineSegment(sketch, "E285", {"start": v(29.05, 28.48) * mm, "end": v(28.98, 28.37) * mm});
            skLineSegment(sketch, "E286", {"start": v(28.98, 28.37) * mm, "end": v(28.91, 28.26) * mm});
            skLineSegment(sketch, "E287", {"start": v(28.91, 28.26) * mm, "end": v(30.34, 26.72) * mm});
            skLineSegment(sketch, "E288", {"start": v(30.34, 26.72) * mm, "end": v(30.46, 26.78) * mm});
            skLineSegment(sketch, "E289", {"start": v(30.46, 26.78) * mm, "end": v(30.58, 26.84) * mm});
            skLineSegment(sketch, "E290", {"start": v(30.58, 26.84) * mm, "end": v(30.81, 26.96) * mm});
            skLineSegment(sketch, "E291", {"start": v(30.81, 26.96) * mm, "end": v(31.3, 27.18) * mm});
            skLineSegment(sketch, "E292", {"start": v(31.3, 27.18) * mm, "end": v(31.8, 27.38) * mm});
            skLineSegment(sketch, "E293", {"start": v(31.8, 27.38) * mm, "end": v(32.32, 27.57) * mm});
            skLineSegment(sketch, "E294", {"start": v(32.32, 27.57) * mm, "end": v(32.85, 27.74) * mm});
            skLineSegment(sketch, "E295", {"start": v(32.85, 27.74) * mm, "end": v(33.39, 27.9) * mm});
            skLineSegment(sketch, "E296", {"start": v(33.39, 27.9) * mm, "end": v(34.62, 26.35) * mm});
            skLineSegment(sketch, "E297", {"start": v(34.62, 26.35) * mm, "end": v(34.35, 25.85) * mm});
            skLineSegment(sketch, "E298", {"start": v(34.35, 25.85) * mm, "end": v(34.07, 25.37) * mm});
            skLineSegment(sketch, "E299", {"start": v(34.07, 25.37) * mm, "end": v(33.77, 24.91) * mm});
            skLineSegment(sketch, "E300", {"start": v(33.77, 24.91) * mm, "end": v(33.46, 24.47) * mm});
            skLineSegment(sketch, "E301", {"start": v(33.46, 24.47) * mm, "end": v(33.14, 24.04) * mm});
            skLineSegment(sketch, "E302", {"start": v(33.14, 24.04) * mm, "end": v(32.97, 23.84) * mm});
            skLineSegment(sketch, "E303", {"start": v(32.97, 23.84) * mm, "end": v(32.89, 23.74) * mm});
            skLineSegment(sketch, "E304", {"start": v(32.89, 23.74) * mm, "end": v(32.8, 23.64) * mm});
            skLineSegment(sketch, "E305", {"start": v(32.8, 23.64) * mm, "end": v(33.99, 21.9) * mm});
            skLineSegment(sketch, "E306", {"start": v(33.99, 21.9) * mm, "end": v(34.1, 21.94) * mm});
            skLineSegment(sketch, "E307", {"start": v(34.1, 21.94) * mm, "end": v(34.23, 21.98) * mm});
            skLineSegment(sketch, "E308", {"start": v(34.23, 21.98) * mm, "end": v(34.49, 22.07) * mm});
            skLineSegment(sketch, "E309", {"start": v(34.49, 22.07) * mm, "end": v(35, 22.21) * mm});
            skLineSegment(sketch, "E310", {"start": v(35, 22.21) * mm, "end": v(35.53, 22.34) * mm});
            skLineSegment(sketch, "E311", {"start": v(35.53, 22.34) * mm, "end": v(36.07, 22.44) * mm});
            skLineSegment(sketch, "E312", {"start": v(36.07, 22.44) * mm, "end": v(36.62, 22.53) * mm});
            skLineSegment(sketch, "E313", {"start": v(36.62, 22.53) * mm, "end": v(37.17, 22.6) * mm});
            skLineSegment(sketch, "E314", {"start": v(37.17, 22.6) * mm, "end": v(38.16, 20.9) * mm});
            skLineSegment(sketch, "E315", {"start": v(38.16, 20.9) * mm, "end": v(37.82, 20.44) * mm});
            skLineSegment(sketch, "E316", {"start": v(37.82, 20.44) * mm, "end": v(37.47, 20.01) * mm});
            skLineSegment(sketch, "E317", {"start": v(37.47, 20.01) * mm, "end": v(37.11, 19.6) * mm});
            skLineSegment(sketch, "E318", {"start": v(37.11, 19.6) * mm, "end": v(36.74, 19.2) * mm});
            skLineSegment(sketch, "E319", {"start": v(36.74, 19.2) * mm, "end": v(36.35, 18.83) * mm});
            skLineSegment(sketch, "E320", {"start": v(36.35, 18.83) * mm, "end": v(36.16, 18.66) * mm});
            skLineSegment(sketch, "E321", {"start": v(36.16, 18.66) * mm, "end": v(36.06, 18.57) * mm});
            skLineSegment(sketch, "E322", {"start": v(36.06, 18.57) * mm, "end": v(35.96, 18.48) * mm});
            skLineSegment(sketch, "E323", {"start": v(35.96, 18.48) * mm, "end": v(36.87, 16.59) * mm});
            skLineSegment(sketch, "E324", {"start": v(36.87, 16.59) * mm, "end": v(37, 16.61) * mm});
            skLineSegment(sketch, "E325", {"start": v(37, 16.61) * mm, "end": v(37.13, 16.64) * mm});
            skLineSegment(sketch, "E326", {"start": v(37.13, 16.64) * mm, "end": v(37.4, 16.68) * mm});
            skLineSegment(sketch, "E327", {"start": v(37.4, 16.68) * mm, "end": v(37.92, 16.75) * mm});
            skLineSegment(sketch, "E328", {"start": v(37.92, 16.75) * mm, "end": v(38.46, 16.8) * mm});
            skLineSegment(sketch, "E329", {"start": v(38.46, 16.8) * mm, "end": v(39.01, 16.82) * mm});
            skLineSegment(sketch, "E330", {"start": v(39.01, 16.82) * mm, "end": v(39.57, 16.82) * mm});
            skLineSegment(sketch, "E331", {"start": v(39.57, 16.82) * mm, "end": v(40.13, 16.81) * mm});
            skLineSegment(sketch, "E332", {"start": v(40.13, 16.81) * mm, "end": v(40.85, 14.97) * mm});
            skLineSegment(sketch, "E333", {"start": v(40.85, 14.97) * mm, "end": v(40.45, 14.58) * mm});
            skLineSegment(sketch, "E334", {"start": v(40.45, 14.58) * mm, "end": v(40.04, 14.2) * mm});
            skLineSegment(sketch, "E335", {"start": v(40.04, 14.2) * mm, "end": v(39.62, 13.85) * mm});
            skLineSegment(sketch, "E336", {"start": v(39.62, 13.85) * mm, "end": v(39.19, 13.52) * mm});
            skLineSegment(sketch, "E337", {"start": v(39.19, 13.52) * mm, "end": v(38.75, 13.2) * mm});
            skLineSegment(sketch, "E338", {"start": v(38.75, 13.2) * mm, "end": v(38.53, 13.06) * mm});
            skLineSegment(sketch, "E339", {"start": v(38.53, 13.06) * mm, "end": v(38.42, 12.99) * mm});
            skLineSegment(sketch, "E340", {"start": v(38.42, 12.99) * mm, "end": v(38.3, 12.92) * mm});
            skLineSegment(sketch, "E341", {"start": v(38.3, 12.92) * mm, "end": v(38.93, 10.9) * mm});
            skLineSegment(sketch, "E342", {"start": v(38.93, 10.9) * mm, "end": v(39.06, 10.91) * mm});
            skLineSegment(sketch, "E343", {"start": v(39.06, 10.91) * mm, "end": v(39.2, 10.92) * mm});
            skLineSegment(sketch, "E344", {"start": v(39.2, 10.92) * mm, "end": v(39.46, 10.92) * mm});
            skLineSegment(sketch, "E345", {"start": v(39.46, 10.92) * mm, "end": v(40, 10.9) * mm});
            skLineSegment(sketch, "E346", {"start": v(40, 10.9) * mm, "end": v(40.54, 10.87) * mm});
            skLineSegment(sketch, "E347", {"start": v(40.54, 10.87) * mm, "end": v(41.08, 10.82) * mm});
            skLineSegment(sketch, "E348", {"start": v(41.08, 10.82) * mm, "end": v(41.63, 10.74) * mm});
            skLineSegment(sketch, "E349", {"start": v(41.63, 10.74) * mm, "end": v(42.19, 10.64) * mm});
            skLineSegment(sketch, "E350", {"start": v(42.19, 10.64) * mm, "end": v(42.63, 8.71) * mm});
            skLineSegment(sketch, "E351", {"start": v(42.63, 8.71) * mm, "end": v(42.17, 8.39) * mm});
            skLineSegment(sketch, "E352", {"start": v(42.17, 8.39) * mm, "end": v(41.7, 8.08) * mm});
            skLineSegment(sketch, "E353", {"start": v(41.7, 8.08) * mm, "end": v(41.24, 7.8) * mm});
            skLineSegment(sketch, "E354", {"start": v(41.24, 7.8) * mm, "end": v(40.77, 7.52) * mm});
            skLineSegment(sketch, "E355", {"start": v(40.77, 7.52) * mm, "end": v(40.29, 7.28) * mm});
            skLineSegment(sketch, "E356", {"start": v(40.29, 7.28) * mm, "end": v(40.05, 7.17) * mm});
            skLineSegment(sketch, "E357", {"start": v(40.05, 7.17) * mm, "end": v(39.93, 7.12) * mm});
            skLineSegment(sketch, "E358", {"start": v(39.93, 7.12) * mm, "end": v(39.8, 7.06) * mm});
            skLineSegment(sketch, "E359", {"start": v(39.8, 7.06) * mm, "end": v(40.12, 4.98) * mm});
            skLineSegment(sketch, "E360", {"start": v(40.12, 4.98) * mm, "end": v(40.25, 4.97) * mm});
            skLineSegment(sketch, "E361", {"start": v(40.25, 4.97) * mm, "end": v(40.38, 4.95) * mm});
            skLineSegment(sketch, "E362", {"start": v(40.38, 4.95) * mm, "end": v(40.65, 4.92) * mm});
            skLineSegment(sketch, "E363", {"start": v(40.65, 4.92) * mm, "end": v(41.17, 4.83) * mm});
            skLineSegment(sketch, "E364", {"start": v(41.17, 4.83) * mm, "end": v(41.7, 4.71) * mm});
            skLineSegment(sketch, "E365", {"start": v(41.7, 4.71) * mm, "end": v(42.23, 4.57) * mm});
            skLineSegment(sketch, "E366", {"start": v(42.23, 4.57) * mm, "end": v(42.77, 4.42) * mm});
            skLineSegment(sketch, "E367", {"start": v(42.77, 4.42) * mm, "end": v(43.3, 4.24) * mm});
            skLineSegment(sketch, "E368", {"start": v(43.3, 4.24) * mm, "end": v(43.45, 2.26) * mm});
            skLineSegment(sketch, "E369", {"start": v(43.45, 2.26) * mm, "end": v(42.95, 2) * mm});
            skLineSegment(sketch, "E370", {"start": v(42.95, 2) * mm, "end": v(42.44, 1.77) * mm});
            skLineSegment(sketch, "E371", {"start": v(42.44, 1.77) * mm, "end": v(41.94, 1.56) * mm});
            skLineSegment(sketch, "E372", {"start": v(41.94, 1.56) * mm, "end": v(41.43, 1.36) * mm});
            skLineSegment(sketch, "E373", {"start": v(41.43, 1.36) * mm, "end": v(40.92, 1.2) * mm});
            skLineSegment(sketch, "E374", {"start": v(40.92, 1.2) * mm, "end": v(40.67, 1.12) * mm});
            skLineSegment(sketch, "E375", {"start": v(40.67, 1.12) * mm, "end": v(40.54, 1.09) * mm});
            skLineSegment(sketch, "E376", {"start": v(40.54, 1.09) * mm, "end": v(40.42, 1.05) * mm});
            skLineSegment(sketch, "E377", {"start": v(40.42, 1.05) * mm, "end": v(40.42, -1.05) * mm});
            skLineSegment(sketch, "E378", {"start": v(40.42, -1.05) * mm, "end": v(40.54, -1.09) * mm});
            skLineSegment(sketch, "E379", {"start": v(40.54, -1.09) * mm, "end": v(40.67, -1.12) * mm});
            skLineSegment(sketch, "E380", {"start": v(40.67, -1.12) * mm, "end": v(40.92, -1.2) * mm});
            skLineSegment(sketch, "E381", {"start": v(40.92, -1.2) * mm, "end": v(41.43, -1.36) * mm});
            skLineSegment(sketch, "E382", {"start": v(41.43, -1.36) * mm, "end": v(41.94, -1.56) * mm});
            skLineSegment(sketch, "E383", {"start": v(41.94, -1.56) * mm, "end": v(42.44, -1.77) * mm});
            skLineSegment(sketch, "E384", {"start": v(42.44, -1.77) * mm, "end": v(42.95, -2) * mm});
            skLineSegment(sketch, "E385", {"start": v(42.95, -2) * mm, "end": v(43.45, -2.26) * mm});
            skLineSegment(sketch, "E386", {"start": v(43.45, -2.26) * mm, "end": v(43.3, -4.24) * mm});
            skLineSegment(sketch, "E387", {"start": v(43.3, -4.24) * mm, "end": v(42.77, -4.41) * mm});
            skLineSegment(sketch, "E388", {"start": v(42.77, -4.41) * mm, "end": v(42.23, -4.57) * mm});
            skLineSegment(sketch, "E389", {"start": v(42.23, -4.57) * mm, "end": v(41.7, -4.71) * mm});
            skLineSegment(sketch, "E390", {"start": v(41.7, -4.71) * mm, "end": v(41.17, -4.83) * mm});
            skLineSegment(sketch, "E391", {"start": v(41.17, -4.83) * mm, "end": v(40.65, -4.92) * mm});
            skLineSegment(sketch, "E392", {"start": v(40.65, -4.92) * mm, "end": v(40.38, -4.95) * mm});
            skLineSegment(sketch, "E393", {"start": v(40.38, -4.95) * mm, "end": v(40.25, -4.97) * mm});
            skLineSegment(sketch, "E394", {"start": v(40.25, -4.97) * mm, "end": v(40.12, -4.98) * mm});
            skLineSegment(sketch, "E395", {"start": v(40.12, -4.98) * mm, "end": v(39.8, -7.06) * mm});
            skLineSegment(sketch, "E396", {"start": v(39.8, -7.06) * mm, "end": v(39.93, -7.12) * mm});
            skLineSegment(sketch, "E397", {"start": v(39.93, -7.12) * mm, "end": v(40.05, -7.17) * mm});
            skLineSegment(sketch, "E398", {"start": v(40.05, -7.17) * mm, "end": v(40.29, -7.28) * mm});
            skLineSegment(sketch, "E399", {"start": v(40.29, -7.28) * mm, "end": v(40.77, -7.52) * mm});
            skLineSegment(sketch, "E400", {"start": v(40.77, -7.52) * mm, "end": v(41.24, -7.8) * mm});
            skLineSegment(sketch, "E401", {"start": v(41.24, -7.8) * mm, "end": v(41.7, -8.08) * mm});
            skLineSegment(sketch, "E402", {"start": v(41.7, -8.08) * mm, "end": v(42.17, -8.39) * mm});
            skLineSegment(sketch, "E403", {"start": v(42.17, -8.39) * mm, "end": v(42.63, -8.71) * mm});
            skLineSegment(sketch, "E404", {"start": v(42.63, -8.71) * mm, "end": v(42.19, -10.64) * mm});
            skLineSegment(sketch, "E405", {"start": v(42.19, -10.64) * mm, "end": v(41.63, -10.74) * mm});
            skLineSegment(sketch, "E406", {"start": v(41.63, -10.74) * mm, "end": v(41.08, -10.82) * mm});
            skLineSegment(sketch, "E407", {"start": v(41.08, -10.82) * mm, "end": v(40.54, -10.87) * mm});
            skLineSegment(sketch, "E408", {"start": v(40.54, -10.87) * mm, "end": v(40, -10.9) * mm});
            skLineSegment(sketch, "E409", {"start": v(40, -10.9) * mm, "end": v(39.46, -10.92) * mm});
            skLineSegment(sketch, "E410", {"start": v(39.46, -10.92) * mm, "end": v(39.2, -10.92) * mm});
            skLineSegment(sketch, "E411", {"start": v(39.2, -10.92) * mm, "end": v(39.06, -10.91) * mm});
            skLineSegment(sketch, "E412", {"start": v(39.06, -10.91) * mm, "end": v(38.93, -10.9) * mm});
            skLineSegment(sketch, "E413", {"start": v(38.93, -10.9) * mm, "end": v(38.3, -12.92) * mm});
            skLineSegment(sketch, "E414", {"start": v(38.3, -12.92) * mm, "end": v(38.42, -12.99) * mm});
            skLineSegment(sketch, "E415", {"start": v(38.42, -12.99) * mm, "end": v(38.53, -13.06) * mm});
            skLineSegment(sketch, "E416", {"start": v(38.53, -13.06) * mm, "end": v(38.75, -13.2) * mm});
            skLineSegment(sketch, "E417", {"start": v(38.75, -13.2) * mm, "end": v(39.19, -13.52) * mm});
            skLineSegment(sketch, "E418", {"start": v(39.19, -13.52) * mm, "end": v(39.62, -13.85) * mm});
            skLineSegment(sketch, "E419", {"start": v(39.62, -13.85) * mm, "end": v(40.04, -14.2) * mm});
            skLineSegment(sketch, "E420", {"start": v(40.04, -14.2) * mm, "end": v(40.45, -14.58) * mm});
            skLineSegment(sketch, "E421", {"start": v(40.45, -14.58) * mm, "end": v(40.85, -14.97) * mm});
            skLineSegment(sketch, "E422", {"start": v(40.85, -14.97) * mm, "end": v(40.13, -16.81) * mm});
            skLineSegment(sketch, "E423", {"start": v(40.13, -16.81) * mm, "end": v(39.57, -16.82) * mm});
            skLineSegment(sketch, "E424", {"start": v(39.57, -16.82) * mm, "end": v(39.01, -16.82) * mm});
            skLineSegment(sketch, "E425", {"start": v(39.01, -16.82) * mm, "end": v(38.46, -16.8) * mm});
            skLineSegment(sketch, "E426", {"start": v(38.46, -16.8) * mm, "end": v(37.92, -16.75) * mm});
            skLineSegment(sketch, "E427", {"start": v(37.92, -16.75) * mm, "end": v(37.4, -16.68) * mm});
            skLineSegment(sketch, "E428", {"start": v(37.4, -16.68) * mm, "end": v(37.13, -16.64) * mm});
            skLineSegment(sketch, "E429", {"start": v(37.13, -16.64) * mm, "end": v(37, -16.61) * mm});
            skLineSegment(sketch, "E430", {"start": v(37, -16.61) * mm, "end": v(36.87, -16.59) * mm});
            skLineSegment(sketch, "E431", {"start": v(36.87, -16.59) * mm, "end": v(35.96, -18.48) * mm});
            skLineSegment(sketch, "E432", {"start": v(35.96, -18.48) * mm, "end": v(36.06, -18.57) * mm});
            skLineSegment(sketch, "E433", {"start": v(36.06, -18.57) * mm, "end": v(36.16, -18.66) * mm});
            skLineSegment(sketch, "E434", {"start": v(36.16, -18.66) * mm, "end": v(36.35, -18.83) * mm});
            skLineSegment(sketch, "E435", {"start": v(36.35, -18.83) * mm, "end": v(36.74, -19.2) * mm});
            skLineSegment(sketch, "E436", {"start": v(36.74, -19.2) * mm, "end": v(37.11, -19.6) * mm});
            skLineSegment(sketch, "E437", {"start": v(37.11, -19.6) * mm, "end": v(37.47, -20.01) * mm});
            skLineSegment(sketch, "E438", {"start": v(37.47, -20.01) * mm, "end": v(37.82, -20.44) * mm});
            skLineSegment(sketch, "E439", {"start": v(37.82, -20.44) * mm, "end": v(38.16, -20.9) * mm});
            skLineSegment(sketch, "E440", {"start": v(38.16, -20.9) * mm, "end": v(37.17, -22.6) * mm});
            skLineSegment(sketch, "E441", {"start": v(37.17, -22.6) * mm, "end": v(36.62, -22.53) * mm});
            skLineSegment(sketch, "E442", {"start": v(36.62, -22.53) * mm, "end": v(36.07, -22.44) * mm});
            skLineSegment(sketch, "E443", {"start": v(36.07, -22.44) * mm, "end": v(35.53, -22.34) * mm});
            skLineSegment(sketch, "E444", {"start": v(35.53, -22.34) * mm, "end": v(35, -22.21) * mm});
            skLineSegment(sketch, "E445", {"start": v(35, -22.21) * mm, "end": v(34.49, -22.07) * mm});
            skLineSegment(sketch, "E446", {"start": v(34.49, -22.07) * mm, "end": v(34.23, -21.98) * mm});
            skLineSegment(sketch, "E447", {"start": v(34.23, -21.98) * mm, "end": v(34.1, -21.94) * mm});
            skLineSegment(sketch, "E448", {"start": v(34.1, -21.94) * mm, "end": v(33.99, -21.9) * mm});
            skLineSegment(sketch, "E449", {"start": v(33.99, -21.9) * mm, "end": v(32.8, -23.64) * mm});
            skLineSegment(sketch, "E450", {"start": v(32.8, -23.64) * mm, "end": v(32.89, -23.74) * mm});
            skLineSegment(sketch, "E451", {"start": v(32.89, -23.74) * mm, "end": v(32.97, -23.84) * mm});
            skLineSegment(sketch, "E452", {"start": v(32.97, -23.84) * mm, "end": v(33.14, -24.04) * mm});
            skLineSegment(sketch, "E453", {"start": v(33.14, -24.04) * mm, "end": v(33.46, -24.47) * mm});
            skLineSegment(sketch, "E454", {"start": v(33.46, -24.47) * mm, "end": v(33.77, -24.91) * mm});
            skLineSegment(sketch, "E455", {"start": v(33.77, -24.91) * mm, "end": v(34.07, -25.37) * mm});
            skLineSegment(sketch, "E456", {"start": v(34.07, -25.37) * mm, "end": v(34.35, -25.85) * mm});
            skLineSegment(sketch, "E457", {"start": v(34.35, -25.85) * mm, "end": v(34.62, -26.35) * mm});
            skLineSegment(sketch, "E458", {"start": v(34.62, -26.35) * mm, "end": v(33.39, -27.9) * mm});
            skLineSegment(sketch, "E459", {"start": v(33.39, -27.9) * mm, "end": v(32.85, -27.74) * mm});
            skLineSegment(sketch, "E460", {"start": v(32.85, -27.74) * mm, "end": v(32.32, -27.57) * mm});
            skLineSegment(sketch, "E461", {"start": v(32.32, -27.57) * mm, "end": v(31.8, -27.38) * mm});
            skLineSegment(sketch, "E462", {"start": v(31.8, -27.38) * mm, "end": v(31.3, -27.18) * mm});
            skLineSegment(sketch, "E463", {"start": v(31.3, -27.18) * mm, "end": v(30.81, -26.96) * mm});
            skLineSegment(sketch, "E464", {"start": v(30.81, -26.96) * mm, "end": v(30.58, -26.84) * mm});
            skLineSegment(sketch, "E465", {"start": v(30.58, -26.84) * mm, "end": v(30.46, -26.78) * mm});
            skLineSegment(sketch, "E466", {"start": v(30.46, -26.78) * mm, "end": v(30.34, -26.72) * mm});
            skLineSegment(sketch, "E467", {"start": v(30.34, -26.72) * mm, "end": v(28.91, -28.26) * mm});
            skLineSegment(sketch, "E468", {"start": v(28.91, -28.26) * mm, "end": v(28.98, -28.37) * mm});
            skLineSegment(sketch, "E469", {"start": v(28.98, -28.37) * mm, "end": v(29.05, -28.48) * mm});
            skLineSegment(sketch, "E470", {"start": v(29.05, -28.48) * mm, "end": v(29.19, -28.71) * mm});
            skLineSegment(sketch, "E471", {"start": v(29.19, -28.71) * mm, "end": v(29.44, -29.18) * mm});
            skLineSegment(sketch, "E472", {"start": v(29.44, -29.18) * mm, "end": v(29.68, -29.67) * mm});
            skLineSegment(sketch, "E473", {"start": v(29.68, -29.67) * mm, "end": v(29.9, -30.17) * mm});
            skLineSegment(sketch, "E474", {"start": v(29.9, -30.17) * mm, "end": v(30.12, -30.68) * mm});
            skLineSegment(sketch, "E475", {"start": v(30.12, -30.68) * mm, "end": v(30.31, -31.21) * mm});
            skLineSegment(sketch, "E476", {"start": v(30.31, -31.21) * mm, "end": v(28.86, -32.56) * mm});
            skLineSegment(sketch, "E477", {"start": v(28.86, -32.56) * mm, "end": v(28.35, -32.33) * mm});
            skLineSegment(sketch, "E478", {"start": v(28.35, -32.33) * mm, "end": v(27.85, -32.08) * mm});
            skLineSegment(sketch, "E479", {"start": v(27.85, -32.08) * mm, "end": v(27.37, -31.82) * mm});
            skLineSegment(sketch, "E480", {"start": v(27.37, -31.82) * mm, "end": v(26.9, -31.54) * mm});
            skLineSegment(sketch, "E481", {"start": v(26.9, -31.54) * mm, "end": v(26.45, -31.25) * mm});
            skLineSegment(sketch, "E482", {"start": v(26.45, -31.25) * mm, "end": v(26.23, -31.1) * mm});
            skLineSegment(sketch, "E483", {"start": v(26.23, -31.1) * mm, "end": v(26.13, -31.02) * mm});
            skLineSegment(sketch, "E484", {"start": v(26.13, -31.02) * mm, "end": v(26.02, -30.94) * mm});
            skLineSegment(sketch, "E485", {"start": v(26.02, -30.94) * mm, "end": v(24.38, -32.25) * mm});
            skLineSegment(sketch, "E486", {"start": v(24.38, -32.25) * mm, "end": v(24.43, -32.37) * mm});
            skLineSegment(sketch, "E487", {"start": v(24.43, -32.37) * mm, "end": v(24.48, -32.5) * mm});
            skLineSegment(sketch, "E488", {"start": v(24.48, -32.5) * mm, "end": v(24.58, -32.74) * mm});
            skLineSegment(sketch, "E489", {"start": v(24.58, -32.74) * mm, "end": v(24.77, -33.24) * mm});
            skLineSegment(sketch, "E490", {"start": v(24.77, -33.24) * mm, "end": v(24.93, -33.76) * mm});
            skLineSegment(sketch, "E491", {"start": v(24.93, -33.76) * mm, "end": v(25.08, -34.29) * mm});
            skLineSegment(sketch, "E492", {"start": v(25.08, -34.29) * mm, "end": v(25.2, -34.83) * mm});
            skLineSegment(sketch, "E493", {"start": v(25.2, -34.83) * mm, "end": v(25.32, -35.38) * mm});
            skLineSegment(sketch, "E494", {"start": v(25.32, -35.38) * mm, "end": v(23.68, -36.5) * mm});
            skLineSegment(sketch, "E495", {"start": v(23.68, -36.5) * mm, "end": v(23.21, -36.19) * mm});
            skLineSegment(sketch, "E496", {"start": v(23.21, -36.19) * mm, "end": v(22.76, -35.87) * mm});
            skLineSegment(sketch, "E497", {"start": v(22.76, -35.87) * mm, "end": v(22.32, -35.54) * mm});
            skLineSegment(sketch, "E498", {"start": v(22.32, -35.54) * mm, "end": v(21.9, -35.2) * mm});
            skLineSegment(sketch, "E499", {"start": v(21.9, -35.2) * mm, "end": v(21.5, -34.84) * mm});
            skLineSegment(sketch, "E500", {"start": v(21.5, -34.84) * mm, "end": v(21.3, -34.66) * mm});
            skLineSegment(sketch, "E501", {"start": v(21.3, -34.66) * mm, "end": v(21.21, -34.57) * mm});
            skLineSegment(sketch, "E502", {"start": v(21.21, -34.57) * mm, "end": v(21.12, -34.47) * mm});
            skLineSegment(sketch, "E503", {"start": v(21.12, -34.47) * mm, "end": v(19.3, -35.53) * mm});
            skLineSegment(sketch, "E504", {"start": v(19.3, -35.53) * mm, "end": v(19.33, -35.65) * mm});
            skLineSegment(sketch, "E505", {"start": v(19.33, -35.65) * mm, "end": v(19.36, -35.78) * mm});
            skLineSegment(sketch, "E506", {"start": v(19.36, -35.78) * mm, "end": v(19.43, -36.04) * mm});
            skLineSegment(sketch, "E507", {"start": v(19.43, -36.04) * mm, "end": v(19.53, -36.56) * mm});
            skLineSegment(sketch, "E508", {"start": v(19.53, -36.56) * mm, "end": v(19.62, -37.1) * mm});
            skLineSegment(sketch, "E509", {"start": v(19.62, -37.1) * mm, "end": v(19.69, -37.64) * mm});
            skLineSegment(sketch, "E510", {"start": v(19.69, -37.64) * mm, "end": v(19.73, -38.2) * mm});
            skLineSegment(sketch, "E511", {"start": v(19.73, -38.2) * mm, "end": v(19.76, -38.76) * mm});
            skLineSegment(sketch, "E512", {"start": v(19.76, -38.76) * mm, "end": v(17.98, -39.62) * mm});
            skLineSegment(sketch, "E513", {"start": v(17.98, -39.62) * mm, "end": v(17.56, -39.24) * mm});
            skLineSegment(sketch, "E514", {"start": v(17.56, -39.24) * mm, "end": v(17.16, -38.86) * mm});
            skLineSegment(sketch, "E515", {"start": v(17.16, -38.86) * mm, "end": v(16.77, -38.47) * mm});
            skLineSegment(sketch, "E516", {"start": v(16.77, -38.47) * mm, "end": v(16.4, -38.07) * mm});
            skLineSegment(sketch, "E517", {"start": v(16.4, -38.07) * mm, "end": v(16.06, -37.66) * mm});
            skLineSegment(sketch, "E518", {"start": v(16.06, -37.66) * mm, "end": v(15.9, -37.45) * mm});
            skLineSegment(sketch, "E519", {"start": v(15.9, -37.45) * mm, "end": v(15.82, -37.34) * mm});
            skLineSegment(sketch, "E520", {"start": v(15.82, -37.34) * mm, "end": v(15.75, -37.24) * mm});
            skLineSegment(sketch, "E521", {"start": v(15.75, -37.24) * mm, "end": v(13.79, -38) * mm});
            skLineSegment(sketch, "E522", {"start": v(13.79, -38) * mm, "end": v(13.8, -38.14) * mm});
            skLineSegment(sketch, "E523", {"start": v(13.8, -38.14) * mm, "end": v(13.82, -38.27) * mm});
            skLineSegment(sketch, "E524", {"start": v(13.82, -38.27) * mm, "end": v(13.84, -38.53) * mm});
            skLineSegment(sketch, "E525", {"start": v(13.84, -38.53) * mm, "end": v(13.87, -39.07) * mm});
            skLineSegment(sketch, "E526", {"start": v(13.87, -39.07) * mm, "end": v(13.87, -39.6) * mm});
            skLineSegment(sketch, "E527", {"start": v(13.87, -39.6) * mm, "end": v(13.86, -40.16) * mm});
            skLineSegment(sketch, "E528", {"start": v(13.86, -40.16) * mm, "end": v(13.82, -40.71) * mm});
            skLineSegment(sketch, "E529", {"start": v(13.82, -40.71) * mm, "end": v(13.77, -41.27) * mm});
            skLineSegment(sketch, "E530", {"start": v(13.77, -41.27) * mm, "end": v(11.87, -41.86) * mm});
            skLineSegment(sketch, "E531", {"start": v(11.87, -41.86) * mm, "end": v(11.51, -41.42) * mm});
            skLineSegment(sketch, "E532", {"start": v(11.51, -41.42) * mm, "end": v(11.17, -40.99) * mm});
            skLineSegment(sketch, "E533", {"start": v(11.17, -40.99) * mm, "end": v(10.85, -40.54) * mm});
            skLineSegment(sketch, "E534", {"start": v(10.85, -40.54) * mm, "end": v(10.55, -40.1) * mm});
            skLineSegment(sketch, "E535", {"start": v(10.55, -40.1) * mm, "end": v(10.27, -39.63) * mm});
            skLineSegment(sketch, "E536", {"start": v(10.27, -39.63) * mm, "end": v(10.14, -39.4) * mm});
            skLineSegment(sketch, "E537", {"start": v(10.14, -39.4) * mm, "end": v(10.08, -39.28) * mm});
            skLineSegment(sketch, "E538", {"start": v(10.08, -39.28) * mm, "end": v(10.02, -39.17) * mm});
            skLineSegment(sketch, "E539", {"start": v(10.02, -39.17) * mm, "end": v(7.97, -39.64) * mm});
            skLineSegment(sketch, "E540", {"start": v(7.97, -39.64) * mm, "end": v(7.96, -39.77) * mm});
            skLineSegment(sketch, "E541", {"start": v(7.96, -39.77) * mm, "end": v(7.96, -39.9) * mm});
            skLineSegment(sketch, "E542", {"start": v(7.96, -39.9) * mm, "end": v(7.94, -40.16) * mm});
            skLineSegment(sketch, "E543", {"start": v(7.94, -40.16) * mm, "end": v(7.89, -40.7) * mm});
            skLineSegment(sketch, "E544", {"start": v(7.89, -40.7) * mm, "end": v(7.81, -41.23) * mm});
            skLineSegment(sketch, "E545", {"start": v(7.81, -41.23) * mm, "end": v(7.72, -41.77) * mm});
            skLineSegment(sketch, "E546", {"start": v(7.72, -41.77) * mm, "end": v(7.6, -42.32) * mm});
            skLineSegment(sketch, "E547", {"start": v(7.6, -42.32) * mm, "end": v(7.46, -42.86) * mm});
            skLineSegment(sketch, "E548", {"start": v(7.46, -42.86) * mm, "end": v(5.5, -43.16) * mm});
            skLineSegment(sketch, "E549", {"start": v(5.5, -43.16) * mm, "end": v(5.21, -42.68) * mm});
            skLineSegment(sketch, "E550", {"start": v(5.21, -42.68) * mm, "end": v(4.94, -42.2) * mm});
            skLineSegment(sketch, "E551", {"start": v(4.94, -42.2) * mm, "end": v(4.69, -41.7) * mm});
            skLineSegment(sketch, "E552", {"start": v(4.69, -41.7) * mm, "end": v(4.46, -41.21) * mm});
            skLineSegment(sketch, "E553", {"start": v(4.46, -41.21) * mm, "end": v(4.25, -40.72) * mm});
            skLineSegment(sketch, "E554", {"start": v(4.25, -40.72) * mm, "end": v(4.16, -40.47) * mm});
            skLineSegment(sketch, "E555", {"start": v(4.16, -40.47) * mm, "end": v(4.11, -40.35) * mm});
            skLineSegment(sketch, "E556", {"start": v(4.11, -40.35) * mm, "end": v(4.07, -40.22) * mm});
            skLineSegment(sketch, "E557", {"start": v(4.07, -40.22) * mm, "end": v(1.97, -40.38) * mm});
            skLineSegment(sketch, "E558", {"start": v(1.97, -40.38) * mm, "end": v(1.95, -40.51) * mm});
            skLineSegment(sketch, "E559", {"start": v(1.95, -40.51) * mm, "end": v(1.92, -40.64) * mm});
            skLineSegment(sketch, "E560", {"start": v(1.92, -40.64) * mm, "end": v(1.87, -40.9) * mm});
            skLineSegment(sketch, "E561", {"start": v(1.87, -40.9) * mm, "end": v(1.74, -41.42) * mm});
            skLineSegment(sketch, "E562", {"start": v(1.74, -41.42) * mm, "end": v(1.58, -41.94) * mm});
            skLineSegment(sketch, "E563", {"start": v(1.58, -41.94) * mm, "end": v(1.4, -42.46) * mm});
            skLineSegment(sketch, "E564", {"start": v(1.4, -42.46) * mm, "end": v(1.2, -42.98) * mm});
            skLineSegment(sketch, "E565", {"start": v(1.2, -42.98) * mm, "end": v(0.99, -43.5) * mm});
            skLineSegment(sketch, "E566", {"start": v(0.99, -43.5) * mm, "end": v(-0.99, -43.5) * mm});
            skLineSegment(sketch, "E567", {"start": v(-0.99, -43.5) * mm, "end": v(-1.2, -42.98) * mm});
            skLineSegment(sketch, "E568", {"start": v(-1.2, -42.98) * mm, "end": v(-1.4, -42.46) * mm});
            skLineSegment(sketch, "E569", {"start": v(-1.4, -42.46) * mm, "end": v(-1.58, -41.94) * mm});
            skLineSegment(sketch, "E570", {"start": v(-1.58, -41.94) * mm, "end": v(-1.74, -41.42) * mm});
            skLineSegment(sketch, "E571", {"start": v(-1.74, -41.42) * mm, "end": v(-1.87, -40.9) * mm});
            skLineSegment(sketch, "E572", {"start": v(-1.87, -40.9) * mm, "end": v(-1.92, -40.64) * mm});
            skLineSegment(sketch, "E573", {"start": v(-1.92, -40.64) * mm, "end": v(-1.95, -40.51) * mm});
            skLineSegment(sketch, "E574", {"start": v(-1.95, -40.51) * mm, "end": v(-1.97, -40.38) * mm});
            skLineSegment(sketch, "E575", {"start": v(-1.97, -40.38) * mm, "end": v(-4.07, -40.22) * mm});
            skLineSegment(sketch, "E576", {"start": v(-4.07, -40.22) * mm, "end": v(-4.11, -40.35) * mm});
            skLineSegment(sketch, "E577", {"start": v(-4.11, -40.35) * mm, "end": v(-4.16, -40.47) * mm});
            skLineSegment(sketch, "E578", {"start": v(-4.16, -40.47) * mm, "end": v(-4.25, -40.72) * mm});
            skLineSegment(sketch, "E579", {"start": v(-4.25, -40.72) * mm, "end": v(-4.46, -41.21) * mm});
            skLineSegment(sketch, "E580", {"start": v(-4.46, -41.21) * mm, "end": v(-4.69, -41.7) * mm});
            skLineSegment(sketch, "E581", {"start": v(-4.69, -41.7) * mm, "end": v(-4.94, -42.2) * mm});
            skLineSegment(sketch, "E582", {"start": v(-4.94, -42.2) * mm, "end": v(-5.21, -42.68) * mm});
            skLineSegment(sketch, "E583", {"start": v(-5.21, -42.68) * mm, "end": v(-5.5, -43.16) * mm});
            skLineSegment(sketch, "E584", {"start": v(-5.5, -43.16) * mm, "end": v(-7.46, -42.86) * mm});
            skLineSegment(sketch, "E585", {"start": v(-7.46, -42.86) * mm, "end": v(-7.6, -42.32) * mm});
            skLineSegment(sketch, "E586", {"start": v(-7.6, -42.32) * mm, "end": v(-7.72, -41.77) * mm});
            skLineSegment(sketch, "E587", {"start": v(-7.72, -41.77) * mm, "end": v(-7.81, -41.23) * mm});
            skLineSegment(sketch, "E588", {"start": v(-7.81, -41.23) * mm, "end": v(-7.89, -40.7) * mm});
            skLineSegment(sketch, "E589", {"start": v(-7.89, -40.7) * mm, "end": v(-7.94, -40.16) * mm});
            skLineSegment(sketch, "E590", {"start": v(-7.94, -40.16) * mm, "end": v(-7.96, -39.9) * mm});
            skLineSegment(sketch, "E591", {"start": v(-7.96, -39.9) * mm, "end": v(-7.96, -39.77) * mm});
            skLineSegment(sketch, "E592", {"start": v(-7.96, -39.77) * mm, "end": v(-7.97, -39.64) * mm});
            skLineSegment(sketch, "E593", {"start": v(-7.97, -39.64) * mm, "end": v(-10.02, -39.17) * mm});
            skLineSegment(sketch, "E594", {"start": v(-10.02, -39.17) * mm, "end": v(-10.08, -39.28) * mm});
            skLineSegment(sketch, "E595", {"start": v(-10.08, -39.28) * mm, "end": v(-10.14, -39.4) * mm});
            skLineSegment(sketch, "E596", {"start": v(-10.14, -39.4) * mm, "end": v(-10.27, -39.63) * mm});
            skLineSegment(sketch, "E597", {"start": v(-10.27, -39.63) * mm, "end": v(-10.55, -40.1) * mm});
            skLineSegment(sketch, "E598", {"start": v(-10.55, -40.1) * mm, "end": v(-10.85, -40.54) * mm});
            skLineSegment(sketch, "E599", {"start": v(-10.85, -40.54) * mm, "end": v(-11.17, -40.99) * mm});
            skLineSegment(sketch, "E600", {"start": v(-11.17, -40.99) * mm, "end": v(-11.51, -41.42) * mm});
            skLineSegment(sketch, "E601", {"start": v(-11.51, -41.42) * mm, "end": v(-11.87, -41.86) * mm});
            skLineSegment(sketch, "E602", {"start": v(-11.87, -41.86) * mm, "end": v(-13.77, -41.27) * mm});
            skLineSegment(sketch, "E603", {"start": v(-13.77, -41.27) * mm, "end": v(-13.82, -40.71) * mm});
            skLineSegment(sketch, "E604", {"start": v(-13.82, -40.71) * mm, "end": v(-13.86, -40.16) * mm});
            skLineSegment(sketch, "E605", {"start": v(-13.86, -40.16) * mm, "end": v(-13.87, -39.6) * mm});
            skLineSegment(sketch, "E606", {"start": v(-13.87, -39.6) * mm, "end": v(-13.87, -39.07) * mm});
            skLineSegment(sketch, "E607", {"start": v(-13.87, -39.07) * mm, "end": v(-13.84, -38.53) * mm});
            skLineSegment(sketch, "E608", {"start": v(-13.84, -38.53) * mm, "end": v(-13.82, -38.27) * mm});
            skLineSegment(sketch, "E609", {"start": v(-13.82, -38.27) * mm, "end": v(-13.8, -38.14) * mm});
            skLineSegment(sketch, "E610", {"start": v(-13.8, -38.14) * mm, "end": v(-13.79, -38) * mm});
            skLineSegment(sketch, "E611", {"start": v(-13.79, -38) * mm, "end": v(-15.75, -37.24) * mm});
            skLineSegment(sketch, "E612", {"start": v(-15.75, -37.24) * mm, "end": v(-15.82, -37.34) * mm});
            skLineSegment(sketch, "E613", {"start": v(-15.82, -37.34) * mm, "end": v(-15.9, -37.45) * mm});
            skLineSegment(sketch, "E614", {"start": v(-15.9, -37.45) * mm, "end": v(-16.06, -37.66) * mm});
            skLineSegment(sketch, "E615", {"start": v(-16.06, -37.66) * mm, "end": v(-16.4, -38.07) * mm});
            skLineSegment(sketch, "E616", {"start": v(-16.4, -38.07) * mm, "end": v(-16.77, -38.47) * mm});
            skLineSegment(sketch, "E617", {"start": v(-16.77, -38.47) * mm, "end": v(-17.16, -38.86) * mm});
            skLineSegment(sketch, "E618", {"start": v(-17.16, -38.86) * mm, "end": v(-17.56, -39.24) * mm});
            skLineSegment(sketch, "E619", {"start": v(-17.56, -39.24) * mm, "end": v(-17.98, -39.62) * mm});
            skLineSegment(sketch, "E620", {"start": v(-17.98, -39.62) * mm, "end": v(-19.76, -38.76) * mm});
            skLineSegment(sketch, "E621", {"start": v(-19.76, -38.76) * mm, "end": v(-19.73, -38.2) * mm});
            skLineSegment(sketch, "E622", {"start": v(-19.73, -38.2) * mm, "end": v(-19.69, -37.64) * mm});
            skLineSegment(sketch, "E623", {"start": v(-19.69, -37.64) * mm, "end": v(-19.62, -37.1) * mm});
            skLineSegment(sketch, "E624", {"start": v(-19.62, -37.1) * mm, "end": v(-19.53, -36.56) * mm});
            skLineSegment(sketch, "E625", {"start": v(-19.53, -36.56) * mm, "end": v(-19.43, -36.04) * mm});
            skLineSegment(sketch, "E626", {"start": v(-19.43, -36.04) * mm, "end": v(-19.36, -35.78) * mm});
            skLineSegment(sketch, "E627", {"start": v(-19.36, -35.78) * mm, "end": v(-19.33, -35.65) * mm});
            skLineSegment(sketch, "E628", {"start": v(-19.33, -35.65) * mm, "end": v(-19.3, -35.53) * mm});
            skLineSegment(sketch, "E629", {"start": v(-19.3, -35.53) * mm, "end": v(-21.12, -34.47) * mm});
            skLineSegment(sketch, "E630", {"start": v(-21.12, -34.47) * mm, "end": v(-21.21, -34.57) * mm});
            skLineSegment(sketch, "E631", {"start": v(-21.21, -34.57) * mm, "end": v(-21.3, -34.66) * mm});
            skLineSegment(sketch, "E632", {"start": v(-21.3, -34.66) * mm, "end": v(-21.5, -34.84) * mm});
            skLineSegment(sketch, "E633", {"start": v(-21.5, -34.84) * mm, "end": v(-21.9, -35.2) * mm});
            skLineSegment(sketch, "E634", {"start": v(-21.9, -35.2) * mm, "end": v(-22.32, -35.54) * mm});
            skLineSegment(sketch, "E635", {"start": v(-22.32, -35.54) * mm, "end": v(-22.76, -35.87) * mm});
            skLineSegment(sketch, "E636", {"start": v(-22.76, -35.87) * mm, "end": v(-23.21, -36.19) * mm});
            skLineSegment(sketch, "E637", {"start": v(-23.21, -36.19) * mm, "end": v(-23.68, -36.5) * mm});
            skLineSegment(sketch, "E638", {"start": v(-23.68, -36.5) * mm, "end": v(-25.32, -35.38) * mm});
            skLineSegment(sketch, "E639", {"start": v(-25.32, -35.38) * mm, "end": v(-25.2, -34.83) * mm});
            skLineSegment(sketch, "E640", {"start": v(-25.2, -34.83) * mm, "end": v(-25.08, -34.29) * mm});
            skLineSegment(sketch, "E641", {"start": v(-25.08, -34.29) * mm, "end": v(-24.93, -33.76) * mm});
            skLineSegment(sketch, "E642", {"start": v(-24.93, -33.76) * mm, "end": v(-24.77, -33.24) * mm});
            skLineSegment(sketch, "E643", {"start": v(-24.77, -33.24) * mm, "end": v(-24.58, -32.74) * mm});
            skLineSegment(sketch, "E644", {"start": v(-24.58, -32.74) * mm, "end": v(-24.48, -32.5) * mm});
            skLineSegment(sketch, "E645", {"start": v(-24.48, -32.5) * mm, "end": v(-24.43, -32.37) * mm});
            skLineSegment(sketch, "E646", {"start": v(-24.43, -32.37) * mm, "end": v(-24.38, -32.25) * mm});
            skLineSegment(sketch, "E647", {"start": v(-24.38, -32.25) * mm, "end": v(-26.02, -30.94) * mm});
            skLineSegment(sketch, "E648", {"start": v(-26.02, -30.94) * mm, "end": v(-26.13, -31.02) * mm});
            skLineSegment(sketch, "E649", {"start": v(-26.13, -31.02) * mm, "end": v(-26.23, -31.1) * mm});
            skLineSegment(sketch, "E650", {"start": v(-26.23, -31.1) * mm, "end": v(-26.45, -31.25) * mm});
            skLineSegment(sketch, "E651", {"start": v(-26.45, -31.25) * mm, "end": v(-26.9, -31.54) * mm});
            skLineSegment(sketch, "E652", {"start": v(-26.9, -31.54) * mm, "end": v(-27.37, -31.82) * mm});
            skLineSegment(sketch, "E653", {"start": v(-27.37, -31.82) * mm, "end": v(-27.85, -32.08) * mm});
            skLineSegment(sketch, "E654", {"start": v(-27.85, -32.08) * mm, "end": v(-28.35, -32.33) * mm});
            skLineSegment(sketch, "E655", {"start": v(-28.35, -32.33) * mm, "end": v(-28.86, -32.56) * mm});
            skLineSegment(sketch, "E656", {"start": v(-28.86, -32.56) * mm, "end": v(-30.31, -31.21) * mm});
            skLineSegment(sketch, "E657", {"start": v(-30.31, -31.21) * mm, "end": v(-30.12, -30.68) * mm});
            skLineSegment(sketch, "E658", {"start": v(-30.12, -30.68) * mm, "end": v(-29.9, -30.17) * mm});
            skLineSegment(sketch, "E659", {"start": v(-29.9, -30.17) * mm, "end": v(-29.68, -29.67) * mm});
            skLineSegment(sketch, "E660", {"start": v(-29.68, -29.67) * mm, "end": v(-29.44, -29.18) * mm});
            skLineSegment(sketch, "E661", {"start": v(-29.44, -29.18) * mm, "end": v(-29.19, -28.71) * mm});
            skLineSegment(sketch, "E662", {"start": v(-29.19, -28.71) * mm, "end": v(-29.05, -28.48) * mm});
            skLineSegment(sketch, "E663", {"start": v(-29.05, -28.48) * mm, "end": v(-28.98, -28.37) * mm});
            skLineSegment(sketch, "E664", {"start": v(-28.98, -28.37) * mm, "end": v(-28.91, -28.26) * mm});
            skLineSegment(sketch, "E665", {"start": v(-28.91, -28.26) * mm, "end": v(-30.34, -26.72) * mm});
            skLineSegment(sketch, "E666", {"start": v(-30.34, -26.72) * mm, "end": v(-30.46, -26.78) * mm});
            skLineSegment(sketch, "E667", {"start": v(-30.46, -26.78) * mm, "end": v(-30.58, -26.84) * mm});
            skLineSegment(sketch, "E668", {"start": v(-30.58, -26.84) * mm, "end": v(-30.81, -26.96) * mm});
            skLineSegment(sketch, "E669", {"start": v(-30.81, -26.96) * mm, "end": v(-31.3, -27.18) * mm});
            skLineSegment(sketch, "E670", {"start": v(-31.3, -27.18) * mm, "end": v(-31.8, -27.38) * mm});
            skLineSegment(sketch, "E671", {"start": v(-31.8, -27.38) * mm, "end": v(-32.32, -27.57) * mm});
            skLineSegment(sketch, "E672", {"start": v(-32.32, -27.57) * mm, "end": v(-32.85, -27.74) * mm});
            skLineSegment(sketch, "E673", {"start": v(-32.85, -27.74) * mm, "end": v(-33.39, -27.9) * mm});
            skLineSegment(sketch, "E674", {"start": v(-33.39, -27.9) * mm, "end": v(-34.62, -26.35) * mm});
            skLineSegment(sketch, "E675", {"start": v(-34.62, -26.35) * mm, "end": v(-34.35, -25.85) * mm});
            skLineSegment(sketch, "E676", {"start": v(-34.35, -25.85) * mm, "end": v(-34.07, -25.37) * mm});
            skLineSegment(sketch, "E677", {"start": v(-34.07, -25.37) * mm, "end": v(-33.77, -24.91) * mm});
            skLineSegment(sketch, "E678", {"start": v(-33.77, -24.91) * mm, "end": v(-33.46, -24.47) * mm});
            skLineSegment(sketch, "E679", {"start": v(-33.46, -24.47) * mm, "end": v(-33.14, -24.04) * mm});
            skLineSegment(sketch, "E680", {"start": v(-33.14, -24.04) * mm, "end": v(-32.97, -23.84) * mm});
            skLineSegment(sketch, "E681", {"start": v(-32.97, -23.84) * mm, "end": v(-32.89, -23.74) * mm});
            skLineSegment(sketch, "E682", {"start": v(-32.89, -23.74) * mm, "end": v(-32.8, -23.64) * mm});
            skLineSegment(sketch, "E683", {"start": v(-32.8, -23.64) * mm, "end": v(-33.99, -21.9) * mm});
            skLineSegment(sketch, "E684", {"start": v(-33.99, -21.9) * mm, "end": v(-34.1, -21.94) * mm});
            skLineSegment(sketch, "E685", {"start": v(-34.1, -21.94) * mm, "end": v(-34.23, -21.98) * mm});
            skLineSegment(sketch, "E686", {"start": v(-34.23, -21.98) * mm, "end": v(-34.49, -22.07) * mm});
            skLineSegment(sketch, "E687", {"start": v(-34.49, -22.07) * mm, "end": v(-35, -22.21) * mm});
            skLineSegment(sketch, "E688", {"start": v(-35, -22.21) * mm, "end": v(-35.53, -22.34) * mm});
            skLineSegment(sketch, "E689", {"start": v(-35.53, -22.34) * mm, "end": v(-36.07, -22.44) * mm});
            skLineSegment(sketch, "E690", {"start": v(-36.07, -22.44) * mm, "end": v(-36.62, -22.53) * mm});
            skLineSegment(sketch, "E691", {"start": v(-36.62, -22.53) * mm, "end": v(-37.17, -22.6) * mm});
            skLineSegment(sketch, "E692", {"start": v(-37.17, -22.6) * mm, "end": v(-38.16, -20.9) * mm});
            skLineSegment(sketch, "E693", {"start": v(-38.16, -20.9) * mm, "end": v(-37.82, -20.44) * mm});
            skLineSegment(sketch, "E694", {"start": v(-37.82, -20.44) * mm, "end": v(-37.47, -20.01) * mm});
            skLineSegment(sketch, "E695", {"start": v(-37.47, -20.01) * mm, "end": v(-37.11, -19.6) * mm});
            skLineSegment(sketch, "E696", {"start": v(-37.11, -19.6) * mm, "end": v(-36.74, -19.2) * mm});
            skLineSegment(sketch, "E697", {"start": v(-36.74, -19.2) * mm, "end": v(-36.35, -18.83) * mm});
            skLineSegment(sketch, "E698", {"start": v(-36.35, -18.83) * mm, "end": v(-36.16, -18.66) * mm});
            skLineSegment(sketch, "E699", {"start": v(-36.16, -18.66) * mm, "end": v(-36.06, -18.57) * mm});
            skLineSegment(sketch, "E700", {"start": v(-36.06, -18.57) * mm, "end": v(-35.96, -18.48) * mm});
            skLineSegment(sketch, "E701", {"start": v(-35.96, -18.48) * mm, "end": v(-36.87, -16.59) * mm});
            skLineSegment(sketch, "E702", {"start": v(-36.87, -16.59) * mm, "end": v(-37, -16.61) * mm});
            skLineSegment(sketch, "E703", {"start": v(-37, -16.61) * mm, "end": v(-37.13, -16.64) * mm});
            skLineSegment(sketch, "E704", {"start": v(-37.13, -16.64) * mm, "end": v(-37.4, -16.68) * mm});
            skLineSegment(sketch, "E705", {"start": v(-37.4, -16.68) * mm, "end": v(-37.92, -16.75) * mm});
            skLineSegment(sketch, "E706", {"start": v(-37.92, -16.75) * mm, "end": v(-38.46, -16.8) * mm});
            skLineSegment(sketch, "E707", {"start": v(-38.46, -16.8) * mm, "end": v(-39.01, -16.82) * mm});
            skLineSegment(sketch, "E708", {"start": v(-39.01, -16.82) * mm, "end": v(-39.57, -16.82) * mm});
            skLineSegment(sketch, "E709", {"start": v(-39.57, -16.82) * mm, "end": v(-40.13, -16.81) * mm});
            skLineSegment(sketch, "E710", {"start": v(-40.13, -16.81) * mm, "end": v(-40.85, -14.97) * mm});
            skLineSegment(sketch, "E711", {"start": v(-40.85, -14.97) * mm, "end": v(-40.45, -14.58) * mm});
            skLineSegment(sketch, "E712", {"start": v(-40.45, -14.58) * mm, "end": v(-40.04, -14.2) * mm});
            skLineSegment(sketch, "E713", {"start": v(-40.04, -14.2) * mm, "end": v(-39.62, -13.85) * mm});
            skLineSegment(sketch, "E714", {"start": v(-39.62, -13.85) * mm, "end": v(-39.19, -13.52) * mm});
            skLineSegment(sketch, "E715", {"start": v(-39.19, -13.52) * mm, "end": v(-38.75, -13.2) * mm});
            skLineSegment(sketch, "E716", {"start": v(-38.75, -13.2) * mm, "end": v(-38.53, -13.06) * mm});
            skLineSegment(sketch, "E717", {"start": v(-38.53, -13.06) * mm, "end": v(-38.42, -12.99) * mm});
            skLineSegment(sketch, "E718", {"start": v(-38.42, -12.99) * mm, "end": v(-38.3, -12.92) * mm});
            skLineSegment(sketch, "E719", {"start": v(-38.3, -12.92) * mm, "end": v(-38.93, -10.9) * mm});
            skLineSegment(sketch, "E720", {"start": v(-38.93, -10.9) * mm, "end": v(-39.06, -10.91) * mm});
            skLineSegment(sketch, "E721", {"start": v(-39.06, -10.91) * mm, "end": v(-39.2, -10.92) * mm});
            skLineSegment(sketch, "E722", {"start": v(-39.2, -10.92) * mm, "end": v(-39.46, -10.92) * mm});
            skLineSegment(sketch, "E723", {"start": v(-39.46, -10.92) * mm, "end": v(-40, -10.9) * mm});
            skLineSegment(sketch, "E724", {"start": v(-40, -10.9) * mm, "end": v(-40.54, -10.87) * mm});
            skLineSegment(sketch, "E725", {"start": v(-40.54, -10.87) * mm, "end": v(-41.08, -10.82) * mm});
            skLineSegment(sketch, "E726", {"start": v(-41.08, -10.82) * mm, "end": v(-41.63, -10.74) * mm});
            skLineSegment(sketch, "E727", {"start": v(-41.63, -10.74) * mm, "end": v(-42.19, -10.64) * mm});
            skLineSegment(sketch, "E728", {"start": v(-42.19, -10.64) * mm, "end": v(-42.63, -8.71) * mm});
            skLineSegment(sketch, "E729", {"start": v(-42.63, -8.71) * mm, "end": v(-42.17, -8.39) * mm});
            skLineSegment(sketch, "E730", {"start": v(-42.17, -8.39) * mm, "end": v(-41.7, -8.08) * mm});
            skLineSegment(sketch, "E731", {"start": v(-41.7, -8.08) * mm, "end": v(-41.24, -7.8) * mm});
            skLineSegment(sketch, "E732", {"start": v(-41.24, -7.8) * mm, "end": v(-40.77, -7.52) * mm});
            skLineSegment(sketch, "E733", {"start": v(-40.77, -7.52) * mm, "end": v(-40.29, -7.28) * mm});
            skLineSegment(sketch, "E734", {"start": v(-40.29, -7.28) * mm, "end": v(-40.05, -7.17) * mm});
            skLineSegment(sketch, "E735", {"start": v(-40.05, -7.17) * mm, "end": v(-39.93, -7.12) * mm});
            skLineSegment(sketch, "E736", {"start": v(-39.93, -7.12) * mm, "end": v(-39.8, -7.06) * mm});
            skLineSegment(sketch, "E737", {"start": v(-39.8, -7.06) * mm, "end": v(-40.12, -4.98) * mm});
            skLineSegment(sketch, "E738", {"start": v(-40.12, -4.98) * mm, "end": v(-40.25, -4.97) * mm});
            skLineSegment(sketch, "E739", {"start": v(-40.25, -4.97) * mm, "end": v(-40.38, -4.95) * mm});
            skLineSegment(sketch, "E740", {"start": v(-40.38, -4.95) * mm, "end": v(-40.65, -4.92) * mm});
            skLineSegment(sketch, "E741", {"start": v(-40.65, -4.92) * mm, "end": v(-41.17, -4.83) * mm});
            skLineSegment(sketch, "E742", {"start": v(-41.17, -4.83) * mm, "end": v(-41.7, -4.71) * mm});
            skLineSegment(sketch, "E743", {"start": v(-41.7, -4.71) * mm, "end": v(-42.23, -4.57) * mm});
            skLineSegment(sketch, "E744", {"start": v(-42.23, -4.57) * mm, "end": v(-42.77, -4.41) * mm});
            skLineSegment(sketch, "E745", {"start": v(-42.77, -4.41) * mm, "end": v(-43.3, -4.24) * mm});
            skLineSegment(sketch, "E746", {"start": v(-43.3, -4.24) * mm, "end": v(-43.45, -2.26) * mm});
            skLineSegment(sketch, "E747", {"start": v(-43.45, -2.26) * mm, "end": v(-42.95, -2) * mm});
            skLineSegment(sketch, "E748", {"start": v(-42.95, -2) * mm, "end": v(-42.44, -1.77) * mm});
            skLineSegment(sketch, "E749", {"start": v(-42.44, -1.77) * mm, "end": v(-41.94, -1.56) * mm});
            skLineSegment(sketch, "E750", {"start": v(-41.94, -1.56) * mm, "end": v(-41.43, -1.36) * mm});
            skLineSegment(sketch, "E751", {"start": v(-41.43, -1.36) * mm, "end": v(-40.92, -1.2) * mm});
            skLineSegment(sketch, "E752", {"start": v(-40.92, -1.2) * mm, "end": v(-40.67, -1.12) * mm});
            skLineSegment(sketch, "E753", {"start": v(-40.67, -1.12) * mm, "end": v(-40.54, -1.09) * mm});
            skLineSegment(sketch, "E754", {"start": v(-40.54, -1.09) * mm, "end": v(-40.42, -1.05) * mm});
            skLineSegment(sketch, "E755", {"start": v(-40.42, -1.05) * mm, "end": v(-40.42, 1.05) * mm});
            skCircle(sketch, "E756", {"center": v(0, 0) * mm, "radius": 48.28 * mm});
            skLineSegment(sketch, "E757", {"start": v(40.42, 1.05) * mm, "end": v(-40.42, -1.05) * mm, "construction": true});
            skLineSegment(sketch, "E758", {"start": v(-43.45, -2.26) * mm, "end": v(43.45, 2.26) * mm, "construction": true});
            skLineSegment(sketch, "E759", {"start": v(40.12, -4.98) * mm, "end": v(43.45, -2.26) * mm, "construction": true});
            skSolve(sketch);
        }
        {
            var Q0;
            Q0=makeQuery(id+"F0.imprint","IMPRINT",FACE,{"disambiguationData":[TD([[makeQuery(id+"F0.imprint","IMPRINT",EDGE,{"derivedFrom":sQuery(id+"F0.wireOp",EDGE,"E0")}),1.0]])]});
            extrude(context, id + "F1", {"entities" : qUnion([Q0]), "depth" : 3 * mm});
        }
        {
            var Q0;
            Q0=makeQuery(id+"F1.opExtrude","CAP_FACE",FACE,{"disambiguationData":[OSD([sQuery(id+"F0.wireOp",EDGE,"E0"),sQuery(id+"F0.wireOp",EDGE,"E1"),sQuery(id+"F0.wireOp",EDGE,"E2"),sQuery(id+"F0.wireOp",EDGE,"E3"),sQuery(id+"F0.wireOp",EDGE,"E4"),sQuery(id+"F0.wireOp",EDGE,"E5"),sQuery(id+"F0.wireOp",EDGE,"E6"),sQuery(id+"F0.wireOp",EDGE,"E7"),sQuery(id+"F0.wireOp",EDGE,"E8"),sQuery(id+"F0.wireOp",EDGE,"E9"),sQuery(id+"F0.wireOp",EDGE,"E10"),sQuery(id+"F0.wireOp",EDGE,"E11"),sQuery(id+"F0.wireOp",EDGE,"E12"),sQuery(id+"F0.wireOp",EDGE,"E13"),sQuery(id+"F0.wireOp",EDGE,"E14"),sQuery(id+"F0.wireOp",EDGE,"E15"),sQuery(id+"F0.wireOp",EDGE,"E16"),sQuery(id+"F0.wireOp",EDGE,"E17"),sQuery(id+"F0.wireOp",EDGE,"E18"),sQuery(id+"F0.wireOp",EDGE,"E19"),sQuery(id+"F0.wireOp",EDGE,"E20"),sQuery(id+"F0.wireOp",EDGE,"E21"),sQuery(id+"F0.wireOp",EDGE,"E22"),sQuery(id+"F0.wireOp",EDGE,"E23"),sQuery(id+"F0.wireOp",EDGE,"E24"),sQuery(id+"F0.wireOp",EDGE,"E25"),sQuery(id+"F0.wireOp",EDGE,"E26"),sQuery(id+"F0.wireOp",EDGE,"E27"),sQuery(id+"F0.wireOp",EDGE,"E28"),sQuery(id+"F0.wireOp",EDGE,"E29"),sQuery(id+"F0.wireOp",EDGE,"E30"),sQuery(id+"F0.wireOp",EDGE,"E31"),sQuery(id+"F0.wireOp",EDGE,"E32"),sQuery(id+"F0.wireOp",EDGE,"E33"),sQuery(id+"F0.wireOp",EDGE,"E34"),sQuery(id+"F0.wireOp",EDGE,"E35"),sQuery(id+"F0.wireOp",EDGE,"E36"),sQuery(id+"F0.wireOp",EDGE,"E37"),sQuery(id+"F0.wireOp",EDGE,"E38"),sQuery(id+"F0.wireOp",EDGE,"E39"),sQuery(id+"F0.wireOp",EDGE,"E40"),sQuery(id+"F0.wireOp",EDGE,"E41"),sQuery(id+"F0.wireOp",EDGE,"E42"),sQuery(id+"F0.wireOp",EDGE,"E43"),sQuery(id+"F0.wireOp",EDGE,"E44"),sQuery(id+"F0.wireOp",EDGE,"E45"),sQuery(id+"F0.wireOp",EDGE,"E46"),sQuery(id+"F0.wireOp",EDGE,"E47"),sQuery(id+"F0.wireOp",EDGE,"E48"),sQuery(id+"F0.wireOp",EDGE,"E49"),sQuery(id+"F0.wireOp",EDGE,"E50"),sQuery(id+"F0.wireOp",EDGE,"E51"),sQuery(id+"F0.wireOp",EDGE,"E52"),sQuery(id+"F0.wireOp",EDGE,"E53"),sQuery(id+"F0.wireOp",EDGE,"E54"),sQuery(id+"F0.wireOp",EDGE,"E55"),sQuery(id+"F0.wireOp",EDGE,"E56"),sQuery(id+"F0.wireOp",EDGE,"E57"),sQuery(id+"F0.wireOp",EDGE,"E58"),sQuery(id+"F0.wireOp",EDGE,"E59"),sQuery(id+"F0.wireOp",EDGE,"E60"),sQuery(id+"F0.wireOp",EDGE,"E61"),sQuery(id+"F0.wireOp",EDGE,"E62"),sQuery(id+"F0.wireOp",EDGE,"E63"),sQuery(id+"F0.wireOp",EDGE,"E64"),sQuery(id+"F0.wireOp",EDGE,"E65"),sQuery(id+"F0.wireOp",EDGE,"E66"),sQuery(id+"F0.wireOp",EDGE,"E67"),sQuery(id+"F0.wireOp",EDGE,"E68"),sQuery(id+"F0.wireOp",EDGE,"E69"),sQuery(id+"F0.wireOp",EDGE,"E70"),sQuery(id+"F0.wireOp",EDGE,"E71"),sQuery(id+"F0.wireOp",EDGE,"E72"),sQuery(id+"F0.wireOp",EDGE,"E73"),sQuery(id+"F0.wireOp",EDGE,"E74"),sQuery(id+"F0.wireOp",EDGE,"E75"),sQuery(id+"F0.wireOp",EDGE,"E76"),sQuery(id+"F0.wireOp",EDGE,"E77"),sQuery(id+"F0.wireOp",EDGE,"E78"),sQuery(id+"F0.wireOp",EDGE,"E79"),sQuery(id+"F0.wireOp",EDGE,"E80"),sQuery(id+"F0.wireOp",EDGE,"E81"),sQuery(id+"F0.wireOp",EDGE,"E82"),sQuery(id+"F0.wireOp",EDGE,"E83"),sQuery(id+"F0.wireOp",EDGE,"E84"),sQuery(id+"F0.wireOp",EDGE,"E85"),sQuery(id+"F0.wireOp",EDGE,"E86"),sQuery(id+"F0.wireOp",EDGE,"E87"),sQuery(id+"F0.wireOp",EDGE,"E88"),sQuery(id+"F0.wireOp",EDGE,"E89"),sQuery(id+"F0.wireOp",EDGE,"E90"),sQuery(id+"F0.wireOp",EDGE,"E91"),sQuery(id+"F0.wireOp",EDGE,"E92"),sQuery(id+"F0.wireOp",EDGE,"E93"),sQuery(id+"F0.wireOp",EDGE,"E94"),sQuery(id+"F0.wireOp",EDGE,"E95"),sQuery(id+"F0.wireOp",EDGE,"E96"),sQuery(id+"F0.wireOp",EDGE,"E97"),sQuery(id+"F0.wireOp",EDGE,"E98"),sQuery(id+"F0.wireOp",EDGE,"E99"),sQuery(id+"F0.wireOp",EDGE,"E100"),sQuery(id+"F0.wireOp",EDGE,"E101"),sQuery(id+"F0.wireOp",EDGE,"E102"),sQuery(id+"F0.wireOp",EDGE,"E103"),sQuery(id+"F0.wireOp",EDGE,"E104"),sQuery(id+"F0.wireOp",EDGE,"E105"),sQuery(id+"F0.wireOp",EDGE,"E106"),sQuery(id+"F0.wireOp",EDGE,"E107"),sQuery(id+"F0.wireOp",EDGE,"E108"),sQuery(id+"F0.wireOp",EDGE,"E109"),sQuery(id+"F0.wireOp",EDGE,"E110"),sQuery(id+"F0.wireOp",EDGE,"E111"),sQuery(id+"F0.wireOp",EDGE,"E112"),sQuery(id+"F0.wireOp",EDGE,"E113"),sQuery(id+"F0.wireOp",EDGE,"E114"),sQuery(id+"F0.wireOp",EDGE,"E115"),sQuery(id+"F0.wireOp",EDGE,"E116"),sQuery(id+"F0.wireOp",EDGE,"E117"),sQuery(id+"F0.wireOp",EDGE,"E118"),sQuery(id+"F0.wireOp",EDGE,"E119"),sQuery(id+"F0.wireOp",EDGE,"E120"),sQuery(id+"F0.wireOp",EDGE,"E121"),sQuery(id+"F0.wireOp",EDGE,"E122"),sQuery(id+"F0.wireOp",EDGE,"E123"),sQuery(id+"F0.wireOp",EDGE,"E124"),sQuery(id+"F0.wireOp",EDGE,"E125"),sQuery(id+"F0.wireOp",EDGE,"E126"),sQuery(id+"F0.wireOp",EDGE,"E127"),sQuery(id+"F0.wireOp",EDGE,"E128"),sQuery(id+"F0.wireOp",EDGE,"E129"),sQuery(id+"F0.wireOp",EDGE,"E130"),sQuery(id+"F0.wireOp",EDGE,"E131"),sQuery(id+"F0.wireOp",EDGE,"E132"),sQuery(id+"F0.wireOp",EDGE,"E133"),sQuery(id+"F0.wireOp",EDGE,"E134"),sQuery(id+"F0.wireOp",EDGE,"E135"),sQuery(id+"F0.wireOp",EDGE,"E136"),sQuery(id+"F0.wireOp",EDGE,"E137"),sQuery(id+"F0.wireOp",EDGE,"E138"),sQuery(id+"F0.wireOp",EDGE,"E139"),sQuery(id+"F0.wireOp",EDGE,"E140"),sQuery(id+"F0.wireOp",EDGE,"E141"),sQuery(id+"F0.wireOp",EDGE,"E142"),sQuery(id+"F0.wireOp",EDGE,"E143"),sQuery(id+"F0.wireOp",EDGE,"E144"),sQuery(id+"F0.wireOp",EDGE,"E145"),sQuery(id+"F0.wireOp",EDGE,"E146"),sQuery(id+"F0.wireOp",EDGE,"E147"),sQuery(id+"F0.wireOp",EDGE,"E148"),sQuery(id+"F0.wireOp",EDGE,"E149"),sQuery(id+"F0.wireOp",EDGE,"E150"),sQuery(id+"F0.wireOp",EDGE,"E151"),sQuery(id+"F0.wireOp",EDGE,"E152"),sQuery(id+"F0.wireOp",EDGE,"E153"),sQuery(id+"F0.wireOp",EDGE,"E154"),sQuery(id+"F0.wireOp",EDGE,"E155"),sQuery(id+"F0.wireOp",EDGE,"E156"),sQuery(id+"F0.wireOp",EDGE,"E157"),sQuery(id+"F0.wireOp",EDGE,"E158"),sQuery(id+"F0.wireOp",EDGE,"E159"),sQuery(id+"F0.wireOp",EDGE,"E160"),sQuery(id+"F0.wireOp",EDGE,"E161"),sQuery(id+"F0.wireOp",EDGE,"E162"),sQuery(id+"F0.wireOp",EDGE,"E163"),sQuery(id+"F0.wireOp",EDGE,"E164"),sQuery(id+"F0.wireOp",EDGE,"E165"),sQuery(id+"F0.wireOp",EDGE,"E166"),sQuery(id+"F0.wireOp",EDGE,"E167"),sQuery(id+"F0.wireOp",EDGE,"E168"),sQuery(id+"F0.wireOp",EDGE,"E169"),sQuery(id+"F0.wireOp",EDGE,"E170"),sQuery(id+"F0.wireOp",EDGE,"E171"),sQuery(id+"F0.wireOp",EDGE,"E172"),sQuery(id+"F0.wireOp",EDGE,"E173"),sQuery(id+"F0.wireOp",EDGE,"E174"),sQuery(id+"F0.wireOp",EDGE,"E175"),sQuery(id+"F0.wireOp",EDGE,"E176"),sQuery(id+"F0.wireOp",EDGE,"E177"),sQuery(id+"F0.wireOp",EDGE,"E178"),sQuery(id+"F0.wireOp",EDGE,"E179"),sQuery(id+"F0.wireOp",EDGE,"E180"),sQuery(id+"F0.wireOp",EDGE,"E181"),sQuery(id+"F0.wireOp",EDGE,"E182"),sQuery(id+"F0.wireOp",EDGE,"E183"),sQuery(id+"F0.wireOp",EDGE,"E184"),sQuery(id+"F0.wireOp",EDGE,"E185"),sQuery(id+"F0.wireOp",EDGE,"E186"),sQuery(id+"F0.wireOp",EDGE,"E187"),sQuery(id+"F0.wireOp",EDGE,"E188"),sQuery(id+"F0.wireOp",EDGE,"E189"),sQuery(id+"F0.wireOp",EDGE,"E190"),sQuery(id+"F0.wireOp",EDGE,"E191"),sQuery(id+"F0.wireOp",EDGE,"E192"),sQuery(id+"F0.wireOp",EDGE,"E193"),sQuery(id+"F0.wireOp",EDGE,"E194"),sQuery(id+"F0.wireOp",EDGE,"E195"),sQuery(id+"F0.wireOp",EDGE,"E196"),sQuery(id+"F0.wireOp",EDGE,"E197"),sQuery(id+"F0.wireOp",EDGE,"E198"),sQuery(id+"F0.wireOp",EDGE,"E199"),sQuery(id+"F0.wireOp",EDGE,"E200"),sQuery(id+"F0.wireOp",EDGE,"E201"),sQuery(id+"F0.wireOp",EDGE,"E202"),sQuery(id+"F0.wireOp",EDGE,"E203"),sQuery(id+"F0.wireOp",EDGE,"E204"),sQuery(id+"F0.wireOp",EDGE,"E205"),sQuery(id+"F0.wireOp",EDGE,"E206"),sQuery(id+"F0.wireOp",EDGE,"E207"),sQuery(id+"F0.wireOp",EDGE,"E208"),sQuery(id+"F0.wireOp",EDGE,"E209"),sQuery(id+"F0.wireOp",EDGE,"E210"),sQuery(id+"F0.wireOp",EDGE,"E211"),sQuery(id+"F0.wireOp",EDGE,"E212"),sQuery(id+"F0.wireOp",EDGE,"E213"),sQuery(id+"F0.wireOp",EDGE,"E214"),sQuery(id+"F0.wireOp",EDGE,"E215"),sQuery(id+"F0.wireOp",EDGE,"E216"),sQuery(id+"F0.wireOp",EDGE,"E217"),sQuery(id+"F0.wireOp",EDGE,"E218"),sQuery(id+"F0.wireOp",EDGE,"E219"),sQuery(id+"F0.wireOp",EDGE,"E220"),sQuery(id+"F0.wireOp",EDGE,"E221"),sQuery(id+"F0.wireOp",EDGE,"E222"),sQuery(id+"F0.wireOp",EDGE,"E223"),sQuery(id+"F0.wireOp",EDGE,"E224"),sQuery(id+"F0.wireOp",EDGE,"E225"),sQuery(id+"F0.wireOp",EDGE,"E226"),sQuery(id+"F0.wireOp",EDGE,"E227"),sQuery(id+"F0.wireOp",EDGE,"E228"),sQuery(id+"F0.wireOp",EDGE,"E229"),sQuery(id+"F0.wireOp",EDGE,"E230"),sQuery(id+"F0.wireOp",EDGE,"E231"),sQuery(id+"F0.wireOp",EDGE,"E232"),sQuery(id+"F0.wireOp",EDGE,"E233"),sQuery(id+"F0.wireOp",EDGE,"E234"),sQuery(id+"F0.wireOp",EDGE,"E235"),sQuery(id+"F0.wireOp",EDGE,"E236"),sQuery(id+"F0.wireOp",EDGE,"E237"),sQuery(id+"F0.wireOp",EDGE,"E238"),sQuery(id+"F0.wireOp",EDGE,"E239"),sQuery(id+"F0.wireOp",EDGE,"E240"),sQuery(id+"F0.wireOp",EDGE,"E241"),sQuery(id+"F0.wireOp",EDGE,"E242"),sQuery(id+"F0.wireOp",EDGE,"E243"),sQuery(id+"F0.wireOp",EDGE,"E244"),sQuery(id+"F0.wireOp",EDGE,"E245"),sQuery(id+"F0.wireOp",EDGE,"E246"),sQuery(id+"F0.wireOp",EDGE,"E247"),sQuery(id+"F0.wireOp",EDGE,"E248"),sQuery(id+"F0.wireOp",EDGE,"E249"),sQuery(id+"F0.wireOp",EDGE,"E250"),sQuery(id+"F0.wireOp",EDGE,"E251"),sQuery(id+"F0.wireOp",EDGE,"E252"),sQuery(id+"F0.wireOp",EDGE,"E253"),sQuery(id+"F0.wireOp",EDGE,"E254"),sQuery(id+"F0.wireOp",EDGE,"E255"),sQuery(id+"F0.wireOp",EDGE,"E256"),sQuery(id+"F0.wireOp",EDGE,"E257"),sQuery(id+"F0.wireOp",EDGE,"E258"),sQuery(id+"F0.wireOp",EDGE,"E259"),sQuery(id+"F0.wireOp",EDGE,"E260"),sQuery(id+"F0.wireOp",EDGE,"E261"),sQuery(id+"F0.wireOp",EDGE,"E262"),sQuery(id+"F0.wireOp",EDGE,"E263"),sQuery(id+"F0.wireOp",EDGE,"E264"),sQuery(id+"F0.wireOp",EDGE,"E265"),sQuery(id+"F0.wireOp",EDGE,"E266"),sQuery(id+"F0.wireOp",EDGE,"E267"),sQuery(id+"F0.wireOp",EDGE,"E268"),sQuery(id+"F0.wireOp",EDGE,"E269"),sQuery(id+"F0.wireOp",EDGE,"E270"),sQuery(id+"F0.wireOp",EDGE,"E271"),sQuery(id+"F0.wireOp",EDGE,"E272"),sQuery(id+"F0.wireOp",EDGE,"E273"),sQuery(id+"F0.wireOp",EDGE,"E274"),sQuery(id+"F0.wireOp",EDGE,"E275"),sQuery(id+"F0.wireOp",EDGE,"E276"),sQuery(id+"F0.wireOp",EDGE,"E277"),sQuery(id+"F0.wireOp",EDGE,"E278"),sQuery(id+"F0.wireOp",EDGE,"E279"),sQuery(id+"F0.wireOp",EDGE,"E280"),sQuery(id+"F0.wireOp",EDGE,"E281"),sQuery(id+"F0.wireOp",EDGE,"E282"),sQuery(id+"F0.wireOp",EDGE,"E283"),sQuery(id+"F0.wireOp",EDGE,"E284"),sQuery(id+"F0.wireOp",EDGE,"E285"),sQuery(id+"F0.wireOp",EDGE,"E286"),sQuery(id+"F0.wireOp",EDGE,"E287"),sQuery(id+"F0.wireOp",EDGE,"E288"),sQuery(id+"F0.wireOp",EDGE,"E289"),sQuery(id+"F0.wireOp",EDGE,"E290"),sQuery(id+"F0.wireOp",EDGE,"E291"),sQuery(id+"F0.wireOp",EDGE,"E292"),sQuery(id+"F0.wireOp",EDGE,"E293"),sQuery(id+"F0.wireOp",EDGE,"E294"),sQuery(id+"F0.wireOp",EDGE,"E295"),sQuery(id+"F0.wireOp",EDGE,"E296"),sQuery(id+"F0.wireOp",EDGE,"E297"),sQuery(id+"F0.wireOp",EDGE,"E298"),sQuery(id+"F0.wireOp",EDGE,"E299"),sQuery(id+"F0.wireOp",EDGE,"E300"),sQuery(id+"F0.wireOp",EDGE,"E301"),sQuery(id+"F0.wireOp",EDGE,"E302"),sQuery(id+"F0.wireOp",EDGE,"E303"),sQuery(id+"F0.wireOp",EDGE,"E304"),sQuery(id+"F0.wireOp",EDGE,"E305"),sQuery(id+"F0.wireOp",EDGE,"E306"),sQuery(id+"F0.wireOp",EDGE,"E307"),sQuery(id+"F0.wireOp",EDGE,"E308"),sQuery(id+"F0.wireOp",EDGE,"E309"),sQuery(id+"F0.wireOp",EDGE,"E310"),sQuery(id+"F0.wireOp",EDGE,"E311"),sQuery(id+"F0.wireOp",EDGE,"E312"),sQuery(id+"F0.wireOp",EDGE,"E313"),sQuery(id+"F0.wireOp",EDGE,"E314"),sQuery(id+"F0.wireOp",EDGE,"E315"),sQuery(id+"F0.wireOp",EDGE,"E316"),sQuery(id+"F0.wireOp",EDGE,"E317"),sQuery(id+"F0.wireOp",EDGE,"E318"),sQuery(id+"F0.wireOp",EDGE,"E319"),sQuery(id+"F0.wireOp",EDGE,"E320"),sQuery(id+"F0.wireOp",EDGE,"E321"),sQuery(id+"F0.wireOp",EDGE,"E322"),sQuery(id+"F0.wireOp",EDGE,"E323"),sQuery(id+"F0.wireOp",EDGE,"E324"),sQuery(id+"F0.wireOp",EDGE,"E325"),sQuery(id+"F0.wireOp",EDGE,"E326"),sQuery(id+"F0.wireOp",EDGE,"E327"),sQuery(id+"F0.wireOp",EDGE,"E328"),sQuery(id+"F0.wireOp",EDGE,"E329"),sQuery(id+"F0.wireOp",EDGE,"E330"),sQuery(id+"F0.wireOp",EDGE,"E331"),sQuery(id+"F0.wireOp",EDGE,"E332"),sQuery(id+"F0.wireOp",EDGE,"E333"),sQuery(id+"F0.wireOp",EDGE,"E334"),sQuery(id+"F0.wireOp",EDGE,"E335"),sQuery(id+"F0.wireOp",EDGE,"E336"),sQuery(id+"F0.wireOp",EDGE,"E337"),sQuery(id+"F0.wireOp",EDGE,"E338"),sQuery(id+"F0.wireOp",EDGE,"E339"),sQuery(id+"F0.wireOp",EDGE,"E340"),sQuery(id+"F0.wireOp",EDGE,"E341"),sQuery(id+"F0.wireOp",EDGE,"E342"),sQuery(id+"F0.wireOp",EDGE,"E343"),sQuery(id+"F0.wireOp",EDGE,"E344"),sQuery(id+"F0.wireOp",EDGE,"E345"),sQuery(id+"F0.wireOp",EDGE,"E346"),sQuery(id+"F0.wireOp",EDGE,"E347"),sQuery(id+"F0.wireOp",EDGE,"E348"),sQuery(id+"F0.wireOp",EDGE,"E349"),sQuery(id+"F0.wireOp",EDGE,"E350"),sQuery(id+"F0.wireOp",EDGE,"E351"),sQuery(id+"F0.wireOp",EDGE,"E352"),sQuery(id+"F0.wireOp",EDGE,"E353"),sQuery(id+"F0.wireOp",EDGE,"E354"),sQuery(id+"F0.wireOp",EDGE,"E355"),sQuery(id+"F0.wireOp",EDGE,"E356"),sQuery(id+"F0.wireOp",EDGE,"E357"),sQuery(id+"F0.wireOp",EDGE,"E358"),sQuery(id+"F0.wireOp",EDGE,"E359"),sQuery(id+"F0.wireOp",EDGE,"E360"),sQuery(id+"F0.wireOp",EDGE,"E361"),sQuery(id+"F0.wireOp",EDGE,"E362"),sQuery(id+"F0.wireOp",EDGE,"E363"),sQuery(id+"F0.wireOp",EDGE,"E364"),sQuery(id+"F0.wireOp",EDGE,"E365"),sQuery(id+"F0.wireOp",EDGE,"E366"),sQuery(id+"F0.wireOp",EDGE,"E367"),sQuery(id+"F0.wireOp",EDGE,"E368"),sQuery(id+"F0.wireOp",EDGE,"E369"),sQuery(id+"F0.wireOp",EDGE,"E370"),sQuery(id+"F0.wireOp",EDGE,"E371"),sQuery(id+"F0.wireOp",EDGE,"E372"),sQuery(id+"F0.wireOp",EDGE,"E373"),sQuery(id+"F0.wireOp",EDGE,"E374"),sQuery(id+"F0.wireOp",EDGE,"E375"),sQuery(id+"F0.wireOp",EDGE,"E376"),sQuery(id+"F0.wireOp",EDGE,"E377"),sQuery(id+"F0.wireOp",EDGE,"E378"),sQuery(id+"F0.wireOp",EDGE,"E379"),sQuery(id+"F0.wireOp",EDGE,"E380"),sQuery(id+"F0.wireOp",EDGE,"E381"),sQuery(id+"F0.wireOp",EDGE,"E382"),sQuery(id+"F0.wireOp",EDGE,"E383"),sQuery(id+"F0.wireOp",EDGE,"E384"),sQuery(id+"F0.wireOp",EDGE,"E385"),sQuery(id+"F0.wireOp",EDGE,"E386"),sQuery(id+"F0.wireOp",EDGE,"E387"),sQuery(id+"F0.wireOp",EDGE,"E388"),sQuery(id+"F0.wireOp",EDGE,"E389"),sQuery(id+"F0.wireOp",EDGE,"E390"),sQuery(id+"F0.wireOp",EDGE,"E391"),sQuery(id+"F0.wireOp",EDGE,"E392"),sQuery(id+"F0.wireOp",EDGE,"E393"),sQuery(id+"F0.wireOp",EDGE,"E394"),sQuery(id+"F0.wireOp",EDGE,"E395"),sQuery(id+"F0.wireOp",EDGE,"E396"),sQuery(id+"F0.wireOp",EDGE,"E397"),sQuery(id+"F0.wireOp",EDGE,"E398"),sQuery(id+"F0.wireOp",EDGE,"E399"),sQuery(id+"F0.wireOp",EDGE,"E400"),sQuery(id+"F0.wireOp",EDGE,"E401"),sQuery(id+"F0.wireOp",EDGE,"E402"),sQuery(id+"F0.wireOp",EDGE,"E403"),sQuery(id+"F0.wireOp",EDGE,"E404"),sQuery(id+"F0.wireOp",EDGE,"E405"),sQuery(id+"F0.wireOp",EDGE,"E406"),sQuery(id+"F0.wireOp",EDGE,"E407"),sQuery(id+"F0.wireOp",EDGE,"E408"),sQuery(id+"F0.wireOp",EDGE,"E409"),sQuery(id+"F0.wireOp",EDGE,"E410"),sQuery(id+"F0.wireOp",EDGE,"E411"),sQuery(id+"F0.wireOp",EDGE,"E412"),sQuery(id+"F0.wireOp",EDGE,"E413"),sQuery(id+"F0.wireOp",EDGE,"E414"),sQuery(id+"F0.wireOp",EDGE,"E415"),sQuery(id+"F0.wireOp",EDGE,"E416"),sQuery(id+"F0.wireOp",EDGE,"E417"),sQuery(id+"F0.wireOp",EDGE,"E418"),sQuery(id+"F0.wireOp",EDGE,"E419"),sQuery(id+"F0.wireOp",EDGE,"E420"),sQuery(id+"F0.wireOp",EDGE,"E421"),sQuery(id+"F0.wireOp",EDGE,"E422"),sQuery(id+"F0.wireOp",EDGE,"E423"),sQuery(id+"F0.wireOp",EDGE,"E424"),sQuery(id+"F0.wireOp",EDGE,"E425"),sQuery(id+"F0.wireOp",EDGE,"E426"),sQuery(id+"F0.wireOp",EDGE,"E427"),sQuery(id+"F0.wireOp",EDGE,"E428"),sQuery(id+"F0.wireOp",EDGE,"E429"),sQuery(id+"F0.wireOp",EDGE,"E430"),sQuery(id+"F0.wireOp",EDGE,"E431"),sQuery(id+"F0.wireOp",EDGE,"E432"),sQuery(id+"F0.wireOp",EDGE,"E433"),sQuery(id+"F0.wireOp",EDGE,"E434"),sQuery(id+"F0.wireOp",EDGE,"E435"),sQuery(id+"F0.wireOp",EDGE,"E436"),sQuery(id+"F0.wireOp",EDGE,"E437"),sQuery(id+"F0.wireOp",EDGE,"E438"),sQuery(id+"F0.wireOp",EDGE,"E439"),sQuery(id+"F0.wireOp",EDGE,"E440"),sQuery(id+"F0.wireOp",EDGE,"E441"),sQuery(id+"F0.wireOp",EDGE,"E442"),sQuery(id+"F0.wireOp",EDGE,"E443"),sQuery(id+"F0.wireOp",EDGE,"E444"),sQuery(id+"F0.wireOp",EDGE,"E445"),sQuery(id+"F0.wireOp",EDGE,"E446"),sQuery(id+"F0.wireOp",EDGE,"E447"),sQuery(id+"F0.wireOp",EDGE,"E448"),sQuery(id+"F0.wireOp",EDGE,"E449"),sQuery(id+"F0.wireOp",EDGE,"E450"),sQuery(id+"F0.wireOp",EDGE,"E451"),sQuery(id+"F0.wireOp",EDGE,"E452"),sQuery(id+"F0.wireOp",EDGE,"E453"),sQuery(id+"F0.wireOp",EDGE,"E454"),sQuery(id+"F0.wireOp",EDGE,"E455"),sQuery(id+"F0.wireOp",EDGE,"E456"),sQuery(id+"F0.wireOp",EDGE,"E457"),sQuery(id+"F0.wireOp",EDGE,"E458"),sQuery(id+"F0.wireOp",EDGE,"E459"),sQuery(id+"F0.wireOp",EDGE,"E460"),sQuery(id+"F0.wireOp",EDGE,"E461"),sQuery(id+"F0.wireOp",EDGE,"E462"),sQuery(id+"F0.wireOp",EDGE,"E463"),sQuery(id+"F0.wireOp",EDGE,"E464"),sQuery(id+"F0.wireOp",EDGE,"E465"),sQuery(id+"F0.wireOp",EDGE,"E466"),sQuery(id+"F0.wireOp",EDGE,"E467"),sQuery(id+"F0.wireOp",EDGE,"E468"),sQuery(id+"F0.wireOp",EDGE,"E469"),sQuery(id+"F0.wireOp",EDGE,"E470"),sQuery(id+"F0.wireOp",EDGE,"E471"),sQuery(id+"F0.wireOp",EDGE,"E472"),sQuery(id+"F0.wireOp",EDGE,"E473"),sQuery(id+"F0.wireOp",EDGE,"E474"),sQuery(id+"F0.wireOp",EDGE,"E475"),sQuery(id+"F0.wireOp",EDGE,"E476"),sQuery(id+"F0.wireOp",EDGE,"E477"),sQuery(id+"F0.wireOp",EDGE,"E478"),sQuery(id+"F0.wireOp",EDGE,"E479"),sQuery(id+"F0.wireOp",EDGE,"E480"),sQuery(id+"F0.wireOp",EDGE,"E481"),sQuery(id+"F0.wireOp",EDGE,"E482"),sQuery(id+"F0.wireOp",EDGE,"E483"),sQuery(id+"F0.wireOp",EDGE,"E484"),sQuery(id+"F0.wireOp",EDGE,"E485"),sQuery(id+"F0.wireOp",EDGE,"E486"),sQuery(id+"F0.wireOp",EDGE,"E487"),sQuery(id+"F0.wireOp",EDGE,"E488"),sQuery(id+"F0.wireOp",EDGE,"E489"),sQuery(id+"F0.wireOp",EDGE,"E490"),sQuery(id+"F0.wireOp",EDGE,"E491"),sQuery(id+"F0.wireOp",EDGE,"E492"),sQuery(id+"F0.wireOp",EDGE,"E493"),sQuery(id+"F0.wireOp",EDGE,"E494"),sQuery(id+"F0.wireOp",EDGE,"E495"),sQuery(id+"F0.wireOp",EDGE,"E496"),sQuery(id+"F0.wireOp",EDGE,"E497"),sQuery(id+"F0.wireOp",EDGE,"E498"),sQuery(id+"F0.wireOp",EDGE,"E499"),sQuery(id+"F0.wireOp",EDGE,"E500"),sQuery(id+"F0.wireOp",EDGE,"E501"),sQuery(id+"F0.wireOp",EDGE,"E502"),sQuery(id+"F0.wireOp",EDGE,"E503"),sQuery(id+"F0.wireOp",EDGE,"E504"),sQuery(id+"F0.wireOp",EDGE,"E505"),sQuery(id+"F0.wireOp",EDGE,"E506"),sQuery(id+"F0.wireOp",EDGE,"E507"),sQuery(id+"F0.wireOp",EDGE,"E508"),sQuery(id+"F0.wireOp",EDGE,"E509"),sQuery(id+"F0.wireOp",EDGE,"E510"),sQuery(id+"F0.wireOp",EDGE,"E511"),sQuery(id+"F0.wireOp",EDGE,"E512"),sQuery(id+"F0.wireOp",EDGE,"E513"),sQuery(id+"F0.wireOp",EDGE,"E514"),sQuery(id+"F0.wireOp",EDGE,"E515"),sQuery(id+"F0.wireOp",EDGE,"E516"),sQuery(id+"F0.wireOp",EDGE,"E517"),sQuery(id+"F0.wireOp",EDGE,"E518"),sQuery(id+"F0.wireOp",EDGE,"E519"),sQuery(id+"F0.wireOp",EDGE,"E520"),sQuery(id+"F0.wireOp",EDGE,"E521"),sQuery(id+"F0.wireOp",EDGE,"E522"),sQuery(id+"F0.wireOp",EDGE,"E523"),sQuery(id+"F0.wireOp",EDGE,"E524"),sQuery(id+"F0.wireOp",EDGE,"E525"),sQuery(id+"F0.wireOp",EDGE,"E526"),sQuery(id+"F0.wireOp",EDGE,"E527"),sQuery(id+"F0.wireOp",EDGE,"E528"),sQuery(id+"F0.wireOp",EDGE,"E529"),sQuery(id+"F0.wireOp",EDGE,"E530"),sQuery(id+"F0.wireOp",EDGE,"E531"),sQuery(id+"F0.wireOp",EDGE,"E532"),sQuery(id+"F0.wireOp",EDGE,"E533"),sQuery(id+"F0.wireOp",EDGE,"E534"),sQuery(id+"F0.wireOp",EDGE,"E535"),sQuery(id+"F0.wireOp",EDGE,"E536"),sQuery(id+"F0.wireOp",EDGE,"E537"),sQuery(id+"F0.wireOp",EDGE,"E538"),sQuery(id+"F0.wireOp",EDGE,"E539"),sQuery(id+"F0.wireOp",EDGE,"E540"),sQuery(id+"F0.wireOp",EDGE,"E541"),sQuery(id+"F0.wireOp",EDGE,"E542"),sQuery(id+"F0.wireOp",EDGE,"E543"),sQuery(id+"F0.wireOp",EDGE,"E544"),sQuery(id+"F0.wireOp",EDGE,"E545"),sQuery(id+"F0.wireOp",EDGE,"E546"),sQuery(id+"F0.wireOp",EDGE,"E547"),sQuery(id+"F0.wireOp",EDGE,"E548"),sQuery(id+"F0.wireOp",EDGE,"E549"),sQuery(id+"F0.wireOp",EDGE,"E550"),sQuery(id+"F0.wireOp",EDGE,"E551"),sQuery(id+"F0.wireOp",EDGE,"E552"),sQuery(id+"F0.wireOp",EDGE,"E553"),sQuery(id+"F0.wireOp",EDGE,"E554"),sQuery(id+"F0.wireOp",EDGE,"E555"),sQuery(id+"F0.wireOp",EDGE,"E556"),sQuery(id+"F0.wireOp",EDGE,"E557"),sQuery(id+"F0.wireOp",EDGE,"E558"),sQuery(id+"F0.wireOp",EDGE,"E559"),sQuery(id+"F0.wireOp",EDGE,"E560"),sQuery(id+"F0.wireOp",EDGE,"E561"),sQuery(id+"F0.wireOp",EDGE,"E562"),sQuery(id+"F0.wireOp",EDGE,"E563"),sQuery(id+"F0.wireOp",EDGE,"E564"),sQuery(id+"F0.wireOp",EDGE,"E565"),sQuery(id+"F0.wireOp",EDGE,"E566"),sQuery(id+"F0.wireOp",EDGE,"E567"),sQuery(id+"F0.wireOp",EDGE,"E568"),sQuery(id+"F0.wireOp",EDGE,"E569"),sQuery(id+"F0.wireOp",EDGE,"E570"),sQuery(id+"F0.wireOp",EDGE,"E571"),sQuery(id+"F0.wireOp",EDGE,"E572"),sQuery(id+"F0.wireOp",EDGE,"E573"),sQuery(id+"F0.wireOp",EDGE,"E574"),sQuery(id+"F0.wireOp",EDGE,"E575"),sQuery(id+"F0.wireOp",EDGE,"E576"),sQuery(id+"F0.wireOp",EDGE,"E577"),sQuery(id+"F0.wireOp",EDGE,"E578"),sQuery(id+"F0.wireOp",EDGE,"E579"),sQuery(id+"F0.wireOp",EDGE,"E580"),sQuery(id+"F0.wireOp",EDGE,"E581"),sQuery(id+"F0.wireOp",EDGE,"E582"),sQuery(id+"F0.wireOp",EDGE,"E583"),sQuery(id+"F0.wireOp",EDGE,"E584"),sQuery(id+"F0.wireOp",EDGE,"E585"),sQuery(id+"F0.wireOp",EDGE,"E586"),sQuery(id+"F0.wireOp",EDGE,"E587"),sQuery(id+"F0.wireOp",EDGE,"E588"),sQuery(id+"F0.wireOp",EDGE,"E589"),sQuery(id+"F0.wireOp",EDGE,"E590"),sQuery(id+"F0.wireOp",EDGE,"E591"),sQuery(id+"F0.wireOp",EDGE,"E592"),sQuery(id+"F0.wireOp",EDGE,"E593"),sQuery(id+"F0.wireOp",EDGE,"E594"),sQuery(id+"F0.wireOp",EDGE,"E595"),sQuery(id+"F0.wireOp",EDGE,"E596"),sQuery(id+"F0.wireOp",EDGE,"E597"),sQuery(id+"F0.wireOp",EDGE,"E598"),sQuery(id+"F0.wireOp",EDGE,"E599"),sQuery(id+"F0.wireOp",EDGE,"E600"),sQuery(id+"F0.wireOp",EDGE,"E601"),sQuery(id+"F0.wireOp",EDGE,"E602"),sQuery(id+"F0.wireOp",EDGE,"E603"),sQuery(id+"F0.wireOp",EDGE,"E604"),sQuery(id+"F0.wireOp",EDGE,"E605"),sQuery(id+"F0.wireOp",EDGE,"E606"),sQuery(id+"F0.wireOp",EDGE,"E607"),sQuery(id+"F0.wireOp",EDGE,"E608"),sQuery(id+"F0.wireOp",EDGE,"E609"),sQuery(id+"F0.wireOp",EDGE,"E610"),sQuery(id+"F0.wireOp",EDGE,"E611"),sQuery(id+"F0.wireOp",EDGE,"E612"),sQuery(id+"F0.wireOp",EDGE,"E613"),sQuery(id+"F0.wireOp",EDGE,"E614"),sQuery(id+"F0.wireOp",EDGE,"E615"),sQuery(id+"F0.wireOp",EDGE,"E616"),sQuery(id+"F0.wireOp",EDGE,"E617"),sQuery(id+"F0.wireOp",EDGE,"E618"),sQuery(id+"F0.wireOp",EDGE,"E619"),sQuery(id+"F0.wireOp",EDGE,"E620"),sQuery(id+"F0.wireOp",EDGE,"E621"),sQuery(id+"F0.wireOp",EDGE,"E622"),sQuery(id+"F0.wireOp",EDGE,"E623"),sQuery(id+"F0.wireOp",EDGE,"E624"),sQuery(id+"F0.wireOp",EDGE,"E625"),sQuery(id+"F0.wireOp",EDGE,"E626"),sQuery(id+"F0.wireOp",EDGE,"E627"),sQuery(id+"F0.wireOp",EDGE,"E628"),sQuery(id+"F0.wireOp",EDGE,"E629"),sQuery(id+"F0.wireOp",EDGE,"E630"),sQuery(id+"F0.wireOp",EDGE,"E631"),sQuery(id+"F0.wireOp",EDGE,"E632"),sQuery(id+"F0.wireOp",EDGE,"E633"),sQuery(id+"F0.wireOp",EDGE,"E634"),sQuery(id+"F0.wireOp",EDGE,"E635"),sQuery(id+"F0.wireOp",EDGE,"E636"),sQuery(id+"F0.wireOp",EDGE,"E637"),sQuery(id+"F0.wireOp",EDGE,"E638"),sQuery(id+"F0.wireOp",EDGE,"E639"),sQuery(id+"F0.wireOp",EDGE,"E640"),sQuery(id+"F0.wireOp",EDGE,"E641"),sQuery(id+"F0.wireOp",EDGE,"E642"),sQuery(id+"F0.wireOp",EDGE,"E643"),sQuery(id+"F0.wireOp",EDGE,"E644"),sQuery(id+"F0.wireOp",EDGE,"E645"),sQuery(id+"F0.wireOp",EDGE,"E646"),sQuery(id+"F0.wireOp",EDGE,"E647"),sQuery(id+"F0.wireOp",EDGE,"E648"),sQuery(id+"F0.wireOp",EDGE,"E649"),sQuery(id+"F0.wireOp",EDGE,"E650"),sQuery(id+"F0.wireOp",EDGE,"E651"),sQuery(id+"F0.wireOp",EDGE,"E652"),sQuery(id+"F0.wireOp",EDGE,"E653"),sQuery(id+"F0.wireOp",EDGE,"E654"),sQuery(id+"F0.wireOp",EDGE,"E655"),sQuery(id+"F0.wireOp",EDGE,"E656"),sQuery(id+"F0.wireOp",EDGE,"E657"),sQuery(id+"F0.wireOp",EDGE,"E658"),sQuery(id+"F0.wireOp",EDGE,"E659"),sQuery(id+"F0.wireOp",EDGE,"E660"),sQuery(id+"F0.wireOp",EDGE,"E661"),sQuery(id+"F0.wireOp",EDGE,"E662"),sQuery(id+"F0.wireOp",EDGE,"E663"),sQuery(id+"F0.wireOp",EDGE,"E664"),sQuery(id+"F0.wireOp",EDGE,"E665"),sQuery(id+"F0.wireOp",EDGE,"E666"),sQuery(id+"F0.wireOp",EDGE,"E667"),sQuery(id+"F0.wireOp",EDGE,"E668"),sQuery(id+"F0.wireOp",EDGE,"E669"),sQuery(id+"F0.wireOp",EDGE,"E670"),sQuery(id+"F0.wireOp",EDGE,"E671"),sQuery(id+"F0.wireOp",EDGE,"E672"),sQuery(id+"F0.wireOp",EDGE,"E673"),sQuery(id+"F0.wireOp",EDGE,"E674"),sQuery(id+"F0.wireOp",EDGE,"E675"),sQuery(id+"F0.wireOp",EDGE,"E676"),sQuery(id+"F0.wireOp",EDGE,"E677"),sQuery(id+"F0.wireOp",EDGE,"E678"),sQuery(id+"F0.wireOp",EDGE,"E679"),sQuery(id+"F0.wireOp",EDGE,"E680"),sQuery(id+"F0.wireOp",EDGE,"E681"),sQuery(id+"F0.wireOp",EDGE,"E682"),sQuery(id+"F0.wireOp",EDGE,"E683"),sQuery(id+"F0.wireOp",EDGE,"E684"),sQuery(id+"F0.wireOp",EDGE,"E685"),sQuery(id+"F0.wireOp",EDGE,"E686"),sQuery(id+"F0.wireOp",EDGE,"E687"),sQuery(id+"F0.wireOp",EDGE,"E688"),sQuery(id+"F0.wireOp",EDGE,"E689"),sQuery(id+"F0.wireOp",EDGE,"E690"),sQuery(id+"F0.wireOp",EDGE,"E691"),sQuery(id+"F0.wireOp",EDGE,"E692"),sQuery(id+"F0.wireOp",EDGE,"E693"),sQuery(id+"F0.wireOp",EDGE,"E694"),sQuery(id+"F0.wireOp",EDGE,"E695"),sQuery(id+"F0.wireOp",EDGE,"E696"),sQuery(id+"F0.wireOp",EDGE,"E697"),sQuery(id+"F0.wireOp",EDGE,"E698"),sQuery(id+"F0.wireOp",EDGE,"E699"),sQuery(id+"F0.wireOp",EDGE,"E700"),sQuery(id+"F0.wireOp",EDGE,"E701"),sQuery(id+"F0.wireOp",EDGE,"E702"),sQuery(id+"F0.wireOp",EDGE,"E703"),sQuery(id+"F0.wireOp",EDGE,"E704"),sQuery(id+"F0.wireOp",EDGE,"E705"),sQuery(id+"F0.wireOp",EDGE,"E706"),sQuery(id+"F0.wireOp",EDGE,"E707"),sQuery(id+"F0.wireOp",EDGE,"E708"),sQuery(id+"F0.wireOp",EDGE,"E709"),sQuery(id+"F0.wireOp",EDGE,"E710"),sQuery(id+"F0.wireOp",EDGE,"E711"),sQuery(id+"F0.wireOp",EDGE,"E712"),sQuery(id+"F0.wireOp",EDGE,"E713"),sQuery(id+"F0.wireOp",EDGE,"E714"),sQuery(id+"F0.wireOp",EDGE,"E715"),sQuery(id+"F0.wireOp",EDGE,"E716"),sQuery(id+"F0.wireOp",EDGE,"E717"),sQuery(id+"F0.wireOp",EDGE,"E718"),sQuery(id+"F0.wireOp",EDGE,"E719"),sQuery(id+"F0.wireOp",EDGE,"E720"),sQuery(id+"F0.wireOp",EDGE,"E721"),sQuery(id+"F0.wireOp",EDGE,"E722"),sQuery(id+"F0.wireOp",EDGE,"E723"),sQuery(id+"F0.wireOp",EDGE,"E724"),sQuery(id+"F0.wireOp",EDGE,"E725"),sQuery(id+"F0.wireOp",EDGE,"E726"),sQuery(id+"F0.wireOp",EDGE,"E727"),sQuery(id+"F0.wireOp",EDGE,"E728"),sQuery(id+"F0.wireOp",EDGE,"E729"),sQuery(id+"F0.wireOp",EDGE,"E730"),sQuery(id+"F0.wireOp",EDGE,"E731"),sQuery(id+"F0.wireOp",EDGE,"E732"),sQuery(id+"F0.wireOp",EDGE,"E733"),sQuery(id+"F0.wireOp",EDGE,"E734"),sQuery(id+"F0.wireOp",EDGE,"E735"),sQuery(id+"F0.wireOp",EDGE,"E736"),sQuery(id+"F0.wireOp",EDGE,"E737"),sQuery(id+"F0.wireOp",EDGE,"E738"),sQuery(id+"F0.wireOp",EDGE,"E739"),sQuery(id+"F0.wireOp",EDGE,"E740"),sQuery(id+"F0.wireOp",EDGE,"E741"),sQuery(id+"F0.wireOp",EDGE,"E742"),sQuery(id+"F0.wireOp",EDGE,"E743"),sQuery(id+"F0.wireOp",EDGE,"E744"),sQuery(id+"F0.wireOp",EDGE,"E745"),sQuery(id+"F0.wireOp",EDGE,"E746"),sQuery(id+"F0.wireOp",EDGE,"E747"),sQuery(id+"F0.wireOp",EDGE,"E748"),sQuery(id+"F0.wireOp",EDGE,"E749"),sQuery(id+"F0.wireOp",EDGE,"E750"),sQuery(id+"F0.wireOp",EDGE,"E751"),sQuery(id+"F0.wireOp",EDGE,"E752"),sQuery(id+"F0.wireOp",EDGE,"E753"),sQuery(id+"F0.wireOp",EDGE,"E754"),sQuery(id+"F0.wireOp",EDGE,"E755"),sQuery(id+"F0.wireOp",EDGE,"E756")])],"isStart":false});
            var sketch = newSketch(context, id + "F2", { "sketchPlane" : qUnion([Q0])});
            skLineSegment(sketch, "E760", {"start": v(0, 0) * mm, "end": v(61.57, -35.55) * mm, "construction": true});
            skLineSegment(sketch, "E761", {"start": v(0, 0) * mm, "end": v(0, 92) * mm, "construction": true});
            skLineSegment(sketch, "E762.MirrorCS", {"start": v(0, 0) * mm, "end": v(-61.57, -35.55) * mm, "construction": true});
            skCircle(sketch, "E763.0", {"center": v(0, 0) * mm, "radius": 48.28 * mm});
            skCircle(sketch, "E764", {"center": v(0, 50) * mm, "radius": 3.5 * mm, "construction": true});
            skCircle(sketch, "E765", {"center": v(0, 50) * mm, "radius": 1.5 * mm});
            skPoint(sketch, "E766", {"position": v(-5, 48.02) * mm});
            skPoint(sketch, "E767.MirrorP", {"position": v(5, 48.02) * mm});
            skLineSegment(sketch, "E768", {"start": v(-5, 48.02) * mm, "end": v(-5, 50.02) * mm});
            skLineSegment(sketch, "E769.MirrorCS", {"start": v(5, 48.02) * mm, "end": v(5, 50.02) * mm});
            skArc(sketch, "E770", {"start": v(-5, 50.02) * mm, "mid": v(0, 55.02) * mm, "end": v(5, 50.02) * mm});
            skCircle(sketch, "E771", {"center": v(-43.3, -25) * mm, "radius": 1.5 * mm});
            skPoint(sketch, "E772", {"position": v(-39.09, -28.34) * mm});
            skLineSegment(sketch, "E773", {"start": v(-39.09, -28.34) * mm, "end": v(-40.82, -29.34) * mm});
            skLineSegment(sketch, "E774.MirrorCS", {"start": v(-44.09, -19.68) * mm, "end": v(-45.82, -20.68) * mm});
            skArc(sketch, "E775", {"start": v(-40.82, -29.34) * mm, "mid": v(-47.65, -27.51) * mm, "end": v(-45.82, -20.68) * mm});
            skLineSegment(sketch, "E776.MirrorCS", {"start": v(39.09, -28.34) * mm, "end": v(40.82, -29.34) * mm});
            skArc(sketch, "E777.MirrorCS", {"start": v(40.82, -29.34) * mm, "mid": v(47.65, -27.51) * mm, "end": v(45.82, -20.68) * mm});
            skLineSegment(sketch, "E778.MirrorCS", {"start": v(44.09, -19.68) * mm, "end": v(45.82, -20.68) * mm});
            skCircle(sketch, "E779.MirrorC", {"center": v(43.3, -25) * mm, "radius": 1.5 * mm});
            skSolve(sketch);
        }
        {
            var Q0;
            Q0=makeQuery(id+"F2.imprint","IMPRINT",FACE,{"disambiguationData":[TD([[makeQuery(id+"F2.imprint","IMPRINT",EDGE,{"derivedFrom":sQuery(id+"F2.wireOp",EDGE,"E765")}),-1.0]])]});
            var Q1;
            Q1=makeQuery(id+"F2.imprint","IMPRINT",FACE,{"disambiguationData":[TD([[makeQuery(id+"F2.imprint","IMPRINT",EDGE,{"derivedFrom":sQuery(id+"F2.wireOp",EDGE,"E771")}),-1.0]])]});
            var Q2;
            {var subQ1=sQuery(id+"F2.wireOp",EDGE,"E776.MirrorCS");Q2=makeQuery(id+"F2.imprint","IMPRINT",FACE,{"disambiguationData":[TD([[makeQuery(id+"F2.imprint","IMPRINT",EDGE,{"derivedFrom":subQ1}),1.0]])]});}
            extrude(context, id + "F3", {"entities" : qUnion([Q0, Q1, Q2]), "oppositeDirection" : true, "depth" : 3 * mm});
        }
        {
            var Q0;
            Q0=makeQuery(id+"F3.opExtrude","SWEPT_EDGE",EDGE,{"disambiguationData":[OSD([sQuery(id+"F2.wireOp",EDGE,"E763.0"),sQuery(id+"F2.wireOp",EDGE,"E774.MirrorCS")])]});
            var Q1;
            Q1=makeQuery(id+"F3.opExtrude","SWEPT_EDGE",EDGE,{"disambiguationData":[OSD([sQuery(id+"F2.wireOp",EDGE,"E763.0"),sQuery(id+"F2.wireOp",EDGE,"E768")])]});
            var Q2;
            Q2=makeQuery(id+"F3.opExtrude","SWEPT_EDGE",EDGE,{"disambiguationData":[OSD([sQuery(id+"F2.wireOp",EDGE,"E763.0"),sQuery(id+"F2.wireOp",EDGE,"E769.MirrorCS")])]});
            var Q3;
            Q3=makeQuery(id+"F3.opExtrude","SWEPT_EDGE",EDGE,{"disambiguationData":[OSD([sQuery(id+"F2.wireOp",EDGE,"E763.0"),sQuery(id+"F2.wireOp",EDGE,"E778.MirrorCS")])]});
            var Q4;
            Q4=makeQuery(id+"F3.opExtrude","SWEPT_EDGE",EDGE,{"disambiguationData":[OSD([sQuery(id+"F2.wireOp",EDGE,"E763.0"),sQuery(id+"F2.wireOp",EDGE,"E776.MirrorCS")])]});
            var Q5;
            Q5=makeQuery(id+"F3.opExtrude","SWEPT_EDGE",EDGE,{"disambiguationData":[OSD([sQuery(id+"F2.wireOp",EDGE,"E763.0"),sQuery(id+"F2.wireOp",EDGE,"E773")])]});
            fillet(context, id + "F4", {"entities" : qUnion([Q0, Q1, Q2, Q3, Q4, Q5]), "radius" : 5 * mm, "tangentPropagation" : true, "allowEdgeOverflow" : false});
        }
        {
            var Q0;
            Q0=qCreatedBy(makeId("Front.planeOp"),FACE);
            var sketch = newSketch(context, id + "F5", { "sketchPlane" : qUnion([Q0])});
            skCircle(sketch, "E780", {"center": v(0, 0) * mm, "radius": 40.55 * mm});
            skSolve(sketch);
        }
        {
            var Q0;
            Q0=makeQuery(id+"F5.imprint","IMPRINT",FACE,{"disambiguationData":[TD([[makeQuery(id+"F5.imprint","IMPRINT",EDGE,{"derivedFrom":sQuery(id+"F5.wireOp",EDGE,"E780")}),1.0]])]});
            extrude(context, id + "F6", {"entities" : qUnion([Q0]), "operationType" : NewBodyOperationType.REMOVE, "endBound" : BoundingType.THROUGH_ALL, "depth" : 25 * mm});
        }
    });
